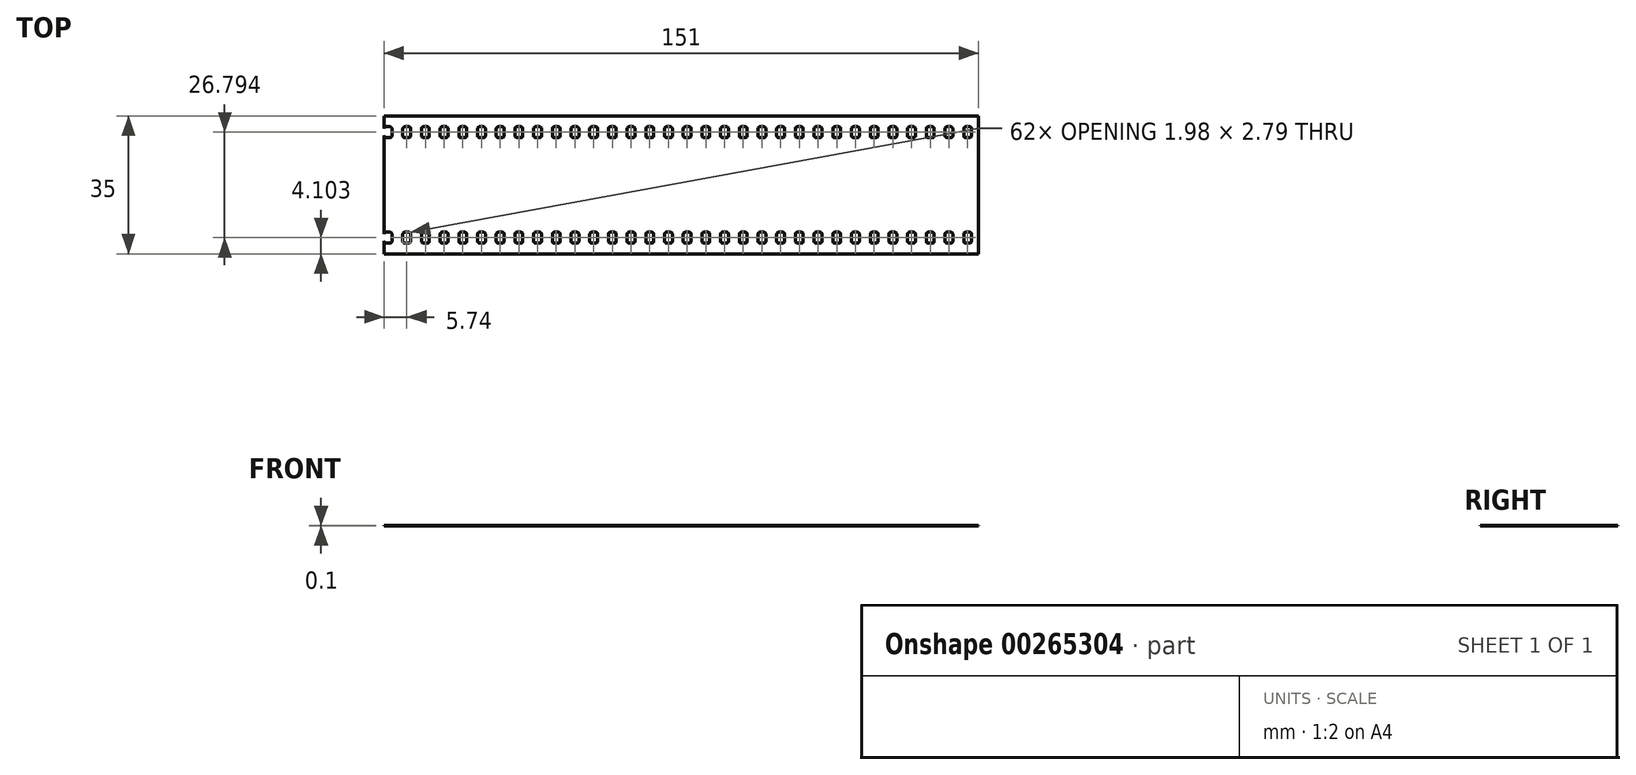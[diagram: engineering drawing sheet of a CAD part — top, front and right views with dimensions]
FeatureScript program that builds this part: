
annotation { "Feature Type Name" : "Feature", "Feature Type Description" : "" }
export const myFeature = defineFeature(function(context is Context, id is Id, definition is map)
    precondition{}
    {
        {
            var Q0;
            Q0=qCreatedBy(makeId("Top.planeOp"),FACE);
            var sketch = newSketch(context, id + "F0", { "sketchPlane" : qUnion([Q0])});
            skLineSegment(sketch, "E0.bottom", {"start": v(0, 0) * mm, "end": v(151, 0) * mm});
            skLineSegment(sketch, "E0.top", {"start": v(0, -35) * mm, "end": v(151, -35) * mm});
            skLineSegment(sketch, "E0.left", {"start": v(0, 0) * mm, "end": v(0, -35) * mm});
            skLineSegment(sketch, "E0.right", {"start": v(151, 0) * mm, "end": v(151, -35) * mm});
            skLineSegment(sketch, "E1.bottom", {"start": v(0.5, -2.7) * mm, "end": v(1.47, -2.7) * mm});
            skLineSegment(sketch, "E1.top", {"start": v(0.5, -5.5) * mm, "end": v(1.47, -5.5) * mm});
            skLineSegment(sketch, "E1.left", {"start": v(0, -3.22) * mm, "end": v(0, -5) * mm});
            skLineSegment(sketch, "E1.right", {"start": v(1.98, -3.22) * mm, "end": v(1.98, -4.99) * mm});
            skPoint(sketch, "E2.visualSharp", {"position": v(0, -2.7) * mm});
            skArc(sketch, "E2.filletArc", {"start": v(0.5, -2.7) * mm, "mid": v(0.15, -2.86) * mm, "end": v(0, -3.22) * mm});
            skPoint(sketch, "E3.visualSharp", {"position": v(1.98, -2.7) * mm});
            skArc(sketch, "E3.filletArc", {"start": v(1.98, -3.22) * mm, "mid": v(1.83, -2.86) * mm, "end": v(1.47, -2.7) * mm});
            skPoint(sketch, "E4.visualSharp", {"position": v(1.98, -5.5) * mm});
            skArc(sketch, "E4.filletArc", {"start": v(1.47, -5.5) * mm, "mid": v(1.83, -5.35) * mm, "end": v(1.98, -4.99) * mm});
            skPoint(sketch, "E5.visualSharp", {"position": v(0, -5.5) * mm});
            skArc(sketch, "E5.filletArc", {"start": v(0, -5) * mm, "mid": v(0.15, -5.35) * mm, "end": v(0.5, -5.5) * mm});
            skPoint(sketch, "E6.0.1.0", {"position": v(0, -32.3) * mm});
            skPoint(sketch, "E6.0.1.1", {"position": v(1.98, -29.5) * mm});
            skPoint(sketch, "E6.0.1.2", {"position": v(0, -29.5) * mm});
            skPoint(sketch, "E6.0.1.3", {"position": v(1.98, -32.3) * mm});
            skLineSegment(sketch, "E6.0.1.4", {"start": v(0.5, -29.5) * mm, "end": v(1.47, -29.5) * mm});
            skLineSegment(sketch, "E6.0.1.5", {"start": v(0.5, -32.3) * mm, "end": v(1.47, -32.3) * mm});
            skLineSegment(sketch, "E6.0.1.6", {"start": v(0, -30) * mm, "end": v(0, -31.78) * mm});
            skLineSegment(sketch, "E6.0.1.7", {"start": v(1.98, -30.01) * mm, "end": v(1.98, -31.78) * mm});
            skArc(sketch, "E6.0.1.8", {"start": v(0.5, -29.5) * mm, "mid": v(0.15, -29.65) * mm, "end": v(0, -30) * mm});
            skArc(sketch, "E6.0.1.9", {"start": v(1.98, -30.01) * mm, "mid": v(1.83, -29.65) * mm, "end": v(1.47, -29.5) * mm});
            skArc(sketch, "E6.0.1.10", {"start": v(1.47, -32.3) * mm, "mid": v(1.83, -32.14) * mm, "end": v(1.98, -31.78) * mm});
            skArc(sketch, "E6.0.1.11", {"start": v(0, -31.78) * mm, "mid": v(0.15, -32.14) * mm, "end": v(0.5, -32.3) * mm});
            skPoint(sketch, "E6.1.0.0", {"position": v(4.75, -5.5) * mm});
            skPoint(sketch, "E6.1.0.1", {"position": v(6.73, -2.7) * mm});
            skPoint(sketch, "E6.1.0.2", {"position": v(4.75, -2.7) * mm});
            skPoint(sketch, "E6.1.0.3", {"position": v(6.73, -5.5) * mm});
            skLineSegment(sketch, "E6.1.0.4", {"start": v(5.26, -2.7) * mm, "end": v(6.22, -2.7) * mm});
            skLineSegment(sketch, "E6.1.0.5", {"start": v(5.26, -5.5) * mm, "end": v(6.22, -5.5) * mm});
            skLineSegment(sketch, "E6.1.0.6", {"start": v(4.75, -3.22) * mm, "end": v(4.75, -5) * mm});
            skLineSegment(sketch, "E6.1.0.7", {"start": v(6.73, -3.22) * mm, "end": v(6.73, -4.99) * mm});
            skArc(sketch, "E6.1.0.8", {"start": v(5.26, -2.7) * mm, "mid": v(4.9, -2.86) * mm, "end": v(4.75, -3.22) * mm});
            skArc(sketch, "E6.1.0.9", {"start": v(6.73, -3.22) * mm, "mid": v(6.58, -2.86) * mm, "end": v(6.22, -2.7) * mm});
            skArc(sketch, "E6.1.0.10", {"start": v(6.22, -5.5) * mm, "mid": v(6.58, -5.35) * mm, "end": v(6.73, -4.99) * mm});
            skArc(sketch, "E6.1.0.11", {"start": v(4.75, -5) * mm, "mid": v(4.9, -5.35) * mm, "end": v(5.26, -5.5) * mm});
            skPoint(sketch, "E6.1.1.0", {"position": v(4.75, -32.3) * mm});
            skPoint(sketch, "E6.1.1.1", {"position": v(6.73, -29.5) * mm});
            skPoint(sketch, "E6.1.1.2", {"position": v(4.75, -29.5) * mm});
            skPoint(sketch, "E6.1.1.3", {"position": v(6.73, -32.3) * mm});
            skLineSegment(sketch, "E6.1.1.4", {"start": v(5.26, -29.5) * mm, "end": v(6.22, -29.5) * mm});
            skLineSegment(sketch, "E6.1.1.5", {"start": v(5.26, -32.3) * mm, "end": v(6.22, -32.3) * mm});
            skLineSegment(sketch, "E6.1.1.6", {"start": v(4.75, -30) * mm, "end": v(4.75, -31.78) * mm});
            skLineSegment(sketch, "E6.1.1.7", {"start": v(6.73, -30.01) * mm, "end": v(6.73, -31.78) * mm});
            skArc(sketch, "E6.1.1.8", {"start": v(5.26, -29.5) * mm, "mid": v(4.9, -29.65) * mm, "end": v(4.75, -30) * mm});
            skArc(sketch, "E6.1.1.9", {"start": v(6.73, -30.01) * mm, "mid": v(6.58, -29.65) * mm, "end": v(6.22, -29.5) * mm});
            skArc(sketch, "E6.1.1.10", {"start": v(6.22, -32.3) * mm, "mid": v(6.58, -32.14) * mm, "end": v(6.73, -31.78) * mm});
            skArc(sketch, "E6.1.1.11", {"start": v(4.75, -31.78) * mm, "mid": v(4.9, -32.14) * mm, "end": v(5.26, -32.3) * mm});
            skPoint(sketch, "E6.2.0.0", {"position": v(9.5, -5.5) * mm});
            skPoint(sketch, "E6.2.0.1", {"position": v(11.48, -2.7) * mm});
            skPoint(sketch, "E6.2.0.2", {"position": v(9.5, -2.7) * mm});
            skPoint(sketch, "E6.2.0.3", {"position": v(11.48, -5.5) * mm});
            skLineSegment(sketch, "E6.2.0.4", {"start": v(10, -2.7) * mm, "end": v(10.97, -2.7) * mm});
            skLineSegment(sketch, "E6.2.0.5", {"start": v(10, -5.5) * mm, "end": v(10.97, -5.5) * mm});
            skLineSegment(sketch, "E6.2.0.6", {"start": v(9.5, -3.22) * mm, "end": v(9.5, -5) * mm});
            skLineSegment(sketch, "E6.2.0.7", {"start": v(11.48, -3.22) * mm, "end": v(11.48, -4.99) * mm});
            skArc(sketch, "E6.2.0.8", {"start": v(10, -2.7) * mm, "mid": v(9.65, -2.86) * mm, "end": v(9.5, -3.22) * mm});
            skArc(sketch, "E6.2.0.9", {"start": v(11.48, -3.22) * mm, "mid": v(11.33, -2.86) * mm, "end": v(10.97, -2.7) * mm});
            skArc(sketch, "E6.2.0.10", {"start": v(10.97, -5.5) * mm, "mid": v(11.33, -5.35) * mm, "end": v(11.48, -4.99) * mm});
            skArc(sketch, "E6.2.0.11", {"start": v(9.5, -5) * mm, "mid": v(9.65, -5.35) * mm, "end": v(10, -5.5) * mm});
            skPoint(sketch, "E6.2.1.0", {"position": v(9.5, -32.3) * mm});
            skPoint(sketch, "E6.2.1.1", {"position": v(11.48, -29.5) * mm});
            skPoint(sketch, "E6.2.1.2", {"position": v(9.5, -29.5) * mm});
            skPoint(sketch, "E6.2.1.3", {"position": v(11.48, -32.3) * mm});
            skLineSegment(sketch, "E6.2.1.4", {"start": v(10, -29.5) * mm, "end": v(10.97, -29.5) * mm});
            skLineSegment(sketch, "E6.2.1.5", {"start": v(10, -32.3) * mm, "end": v(10.97, -32.3) * mm});
            skLineSegment(sketch, "E6.2.1.6", {"start": v(9.5, -30) * mm, "end": v(9.5, -31.78) * mm});
            skLineSegment(sketch, "E6.2.1.7", {"start": v(11.48, -30.01) * mm, "end": v(11.48, -31.78) * mm});
            skArc(sketch, "E6.2.1.8", {"start": v(10, -29.5) * mm, "mid": v(9.65, -29.65) * mm, "end": v(9.5, -30) * mm});
            skArc(sketch, "E6.2.1.9", {"start": v(11.48, -30.01) * mm, "mid": v(11.33, -29.65) * mm, "end": v(10.97, -29.5) * mm});
            skArc(sketch, "E6.2.1.10", {"start": v(10.97, -32.3) * mm, "mid": v(11.33, -32.14) * mm, "end": v(11.48, -31.78) * mm});
            skArc(sketch, "E6.2.1.11", {"start": v(9.5, -31.78) * mm, "mid": v(9.65, -32.14) * mm, "end": v(10, -32.3) * mm});
            skPoint(sketch, "E6.3.0.0", {"position": v(14.25, -5.5) * mm});
            skPoint(sketch, "E6.3.0.1", {"position": v(16.23, -2.7) * mm});
            skPoint(sketch, "E6.3.0.2", {"position": v(14.25, -2.7) * mm});
            skPoint(sketch, "E6.3.0.3", {"position": v(16.23, -5.5) * mm});
            skLineSegment(sketch, "E6.3.0.4", {"start": v(14.76, -2.7) * mm, "end": v(15.72, -2.7) * mm});
            skLineSegment(sketch, "E6.3.0.5", {"start": v(14.76, -5.5) * mm, "end": v(15.72, -5.5) * mm});
            skLineSegment(sketch, "E6.3.0.6", {"start": v(14.25, -3.22) * mm, "end": v(14.25, -5) * mm});
            skLineSegment(sketch, "E6.3.0.7", {"start": v(16.23, -3.22) * mm, "end": v(16.23, -4.99) * mm});
            skArc(sketch, "E6.3.0.8", {"start": v(14.76, -2.7) * mm, "mid": v(14.4, -2.86) * mm, "end": v(14.25, -3.22) * mm});
            skArc(sketch, "E6.3.0.9", {"start": v(16.23, -3.22) * mm, "mid": v(16.08, -2.86) * mm, "end": v(15.72, -2.7) * mm});
            skArc(sketch, "E6.3.0.10", {"start": v(15.72, -5.5) * mm, "mid": v(16.08, -5.35) * mm, "end": v(16.23, -4.99) * mm});
            skArc(sketch, "E6.3.0.11", {"start": v(14.25, -5) * mm, "mid": v(14.4, -5.35) * mm, "end": v(14.76, -5.5) * mm});
            skPoint(sketch, "E6.3.1.0", {"position": v(14.25, -32.3) * mm});
            skPoint(sketch, "E6.3.1.1", {"position": v(16.23, -29.5) * mm});
            skPoint(sketch, "E6.3.1.2", {"position": v(14.25, -29.5) * mm});
            skPoint(sketch, "E6.3.1.3", {"position": v(16.23, -32.3) * mm});
            skLineSegment(sketch, "E6.3.1.4", {"start": v(14.76, -29.5) * mm, "end": v(15.72, -29.5) * mm});
            skLineSegment(sketch, "E6.3.1.5", {"start": v(14.76, -32.3) * mm, "end": v(15.72, -32.3) * mm});
            skLineSegment(sketch, "E6.3.1.6", {"start": v(14.25, -30) * mm, "end": v(14.25, -31.78) * mm});
            skLineSegment(sketch, "E6.3.1.7", {"start": v(16.23, -30.01) * mm, "end": v(16.23, -31.78) * mm});
            skArc(sketch, "E6.3.1.8", {"start": v(14.76, -29.5) * mm, "mid": v(14.4, -29.65) * mm, "end": v(14.25, -30) * mm});
            skArc(sketch, "E6.3.1.9", {"start": v(16.23, -30.01) * mm, "mid": v(16.08, -29.65) * mm, "end": v(15.72, -29.5) * mm});
            skArc(sketch, "E6.3.1.10", {"start": v(15.72, -32.3) * mm, "mid": v(16.08, -32.14) * mm, "end": v(16.23, -31.78) * mm});
            skArc(sketch, "E6.3.1.11", {"start": v(14.25, -31.78) * mm, "mid": v(14.4, -32.14) * mm, "end": v(14.76, -32.3) * mm});
            skPoint(sketch, "E6.4.0.0", {"position": v(19, -5.5) * mm});
            skPoint(sketch, "E6.4.0.1", {"position": v(20.98, -2.7) * mm});
            skPoint(sketch, "E6.4.0.2", {"position": v(19, -2.7) * mm});
            skPoint(sketch, "E6.4.0.3", {"position": v(20.98, -5.5) * mm});
            skLineSegment(sketch, "E6.4.0.4", {"start": v(19.5, -2.7) * mm, "end": v(20.47, -2.7) * mm});
            skLineSegment(sketch, "E6.4.0.5", {"start": v(19.5, -5.5) * mm, "end": v(20.47, -5.5) * mm});
            skLineSegment(sketch, "E6.4.0.6", {"start": v(19, -3.22) * mm, "end": v(19, -5) * mm});
            skLineSegment(sketch, "E6.4.0.7", {"start": v(20.98, -3.22) * mm, "end": v(20.98, -4.99) * mm});
            skArc(sketch, "E6.4.0.8", {"start": v(19.5, -2.7) * mm, "mid": v(19.15, -2.86) * mm, "end": v(19, -3.22) * mm});
            skArc(sketch, "E6.4.0.9", {"start": v(20.98, -3.22) * mm, "mid": v(20.83, -2.86) * mm, "end": v(20.47, -2.7) * mm});
            skArc(sketch, "E6.4.0.10", {"start": v(20.47, -5.5) * mm, "mid": v(20.83, -5.35) * mm, "end": v(20.98, -4.99) * mm});
            skArc(sketch, "E6.4.0.11", {"start": v(19, -5) * mm, "mid": v(19.15, -5.35) * mm, "end": v(19.5, -5.5) * mm});
            skPoint(sketch, "E6.4.1.0", {"position": v(19, -32.3) * mm});
            skPoint(sketch, "E6.4.1.1", {"position": v(20.98, -29.5) * mm});
            skPoint(sketch, "E6.4.1.2", {"position": v(19, -29.5) * mm});
            skPoint(sketch, "E6.4.1.3", {"position": v(20.98, -32.3) * mm});
            skLineSegment(sketch, "E6.4.1.4", {"start": v(19.5, -29.5) * mm, "end": v(20.47, -29.5) * mm});
            skLineSegment(sketch, "E6.4.1.5", {"start": v(19.5, -32.3) * mm, "end": v(20.47, -32.3) * mm});
            skLineSegment(sketch, "E6.4.1.6", {"start": v(19, -30) * mm, "end": v(19, -31.78) * mm});
            skLineSegment(sketch, "E6.4.1.7", {"start": v(20.98, -30.01) * mm, "end": v(20.98, -31.78) * mm});
            skArc(sketch, "E6.4.1.8", {"start": v(19.5, -29.5) * mm, "mid": v(19.15, -29.65) * mm, "end": v(19, -30) * mm});
            skArc(sketch, "E6.4.1.9", {"start": v(20.98, -30.01) * mm, "mid": v(20.83, -29.65) * mm, "end": v(20.47, -29.5) * mm});
            skArc(sketch, "E6.4.1.10", {"start": v(20.47, -32.3) * mm, "mid": v(20.83, -32.14) * mm, "end": v(20.98, -31.78) * mm});
            skArc(sketch, "E6.4.1.11", {"start": v(19, -31.78) * mm, "mid": v(19.15, -32.14) * mm, "end": v(19.5, -32.3) * mm});
            skPoint(sketch, "E6.5.0.0", {"position": v(23.75, -5.5) * mm});
            skPoint(sketch, "E6.5.0.1", {"position": v(25.73, -2.7) * mm});
            skPoint(sketch, "E6.5.0.2", {"position": v(23.75, -2.7) * mm});
            skPoint(sketch, "E6.5.0.3", {"position": v(25.73, -5.5) * mm});
            skLineSegment(sketch, "E6.5.0.4", {"start": v(24.26, -2.7) * mm, "end": v(25.22, -2.7) * mm});
            skLineSegment(sketch, "E6.5.0.5", {"start": v(24.26, -5.5) * mm, "end": v(25.22, -5.5) * mm});
            skLineSegment(sketch, "E6.5.0.6", {"start": v(23.75, -3.22) * mm, "end": v(23.75, -5) * mm});
            skLineSegment(sketch, "E6.5.0.7", {"start": v(25.73, -3.22) * mm, "end": v(25.73, -4.99) * mm});
            skArc(sketch, "E6.5.0.8", {"start": v(24.26, -2.7) * mm, "mid": v(23.9, -2.86) * mm, "end": v(23.75, -3.22) * mm});
            skArc(sketch, "E6.5.0.9", {"start": v(25.73, -3.22) * mm, "mid": v(25.58, -2.86) * mm, "end": v(25.22, -2.7) * mm});
            skArc(sketch, "E6.5.0.10", {"start": v(25.22, -5.5) * mm, "mid": v(25.58, -5.35) * mm, "end": v(25.73, -4.99) * mm});
            skArc(sketch, "E6.5.0.11", {"start": v(23.75, -5) * mm, "mid": v(23.9, -5.35) * mm, "end": v(24.26, -5.5) * mm});
            skPoint(sketch, "E6.5.1.0", {"position": v(23.75, -32.3) * mm});
            skPoint(sketch, "E6.5.1.1", {"position": v(25.73, -29.5) * mm});
            skPoint(sketch, "E6.5.1.2", {"position": v(23.75, -29.5) * mm});
            skPoint(sketch, "E6.5.1.3", {"position": v(25.73, -32.3) * mm});
            skLineSegment(sketch, "E6.5.1.4", {"start": v(24.26, -29.5) * mm, "end": v(25.22, -29.5) * mm});
            skLineSegment(sketch, "E6.5.1.5", {"start": v(24.26, -32.3) * mm, "end": v(25.22, -32.3) * mm});
            skLineSegment(sketch, "E6.5.1.6", {"start": v(23.75, -30) * mm, "end": v(23.75, -31.78) * mm});
            skLineSegment(sketch, "E6.5.1.7", {"start": v(25.73, -30.01) * mm, "end": v(25.73, -31.78) * mm});
            skArc(sketch, "E6.5.1.8", {"start": v(24.26, -29.5) * mm, "mid": v(23.9, -29.65) * mm, "end": v(23.75, -30) * mm});
            skArc(sketch, "E6.5.1.9", {"start": v(25.73, -30.01) * mm, "mid": v(25.58, -29.65) * mm, "end": v(25.22, -29.5) * mm});
            skArc(sketch, "E6.5.1.10", {"start": v(25.22, -32.3) * mm, "mid": v(25.58, -32.14) * mm, "end": v(25.73, -31.78) * mm});
            skArc(sketch, "E6.5.1.11", {"start": v(23.75, -31.78) * mm, "mid": v(23.9, -32.14) * mm, "end": v(24.26, -32.3) * mm});
            skPoint(sketch, "E6.6.0.0", {"position": v(28.5, -5.5) * mm});
            skPoint(sketch, "E6.6.0.1", {"position": v(30.48, -2.7) * mm});
            skPoint(sketch, "E6.6.0.2", {"position": v(28.5, -2.7) * mm});
            skPoint(sketch, "E6.6.0.3", {"position": v(30.48, -5.5) * mm});
            skLineSegment(sketch, "E6.6.0.4", {"start": v(29, -2.7) * mm, "end": v(29.97, -2.7) * mm});
            skLineSegment(sketch, "E6.6.0.5", {"start": v(29, -5.5) * mm, "end": v(29.97, -5.5) * mm});
            skLineSegment(sketch, "E6.6.0.6", {"start": v(28.5, -3.22) * mm, "end": v(28.5, -5) * mm});
            skLineSegment(sketch, "E6.6.0.7", {"start": v(30.48, -3.22) * mm, "end": v(30.48, -4.99) * mm});
            skArc(sketch, "E6.6.0.8", {"start": v(29, -2.7) * mm, "mid": v(28.65, -2.86) * mm, "end": v(28.5, -3.22) * mm});
            skArc(sketch, "E6.6.0.9", {"start": v(30.48, -3.22) * mm, "mid": v(30.33, -2.86) * mm, "end": v(29.97, -2.7) * mm});
            skArc(sketch, "E6.6.0.10", {"start": v(29.97, -5.5) * mm, "mid": v(30.33, -5.35) * mm, "end": v(30.48, -4.99) * mm});
            skArc(sketch, "E6.6.0.11", {"start": v(28.5, -5) * mm, "mid": v(28.65, -5.35) * mm, "end": v(29, -5.5) * mm});
            skPoint(sketch, "E6.6.1.0", {"position": v(28.5, -32.3) * mm});
            skPoint(sketch, "E6.6.1.1", {"position": v(30.48, -29.5) * mm});
            skPoint(sketch, "E6.6.1.2", {"position": v(28.5, -29.5) * mm});
            skPoint(sketch, "E6.6.1.3", {"position": v(30.48, -32.3) * mm});
            skLineSegment(sketch, "E6.6.1.4", {"start": v(29, -29.5) * mm, "end": v(29.97, -29.5) * mm});
            skLineSegment(sketch, "E6.6.1.5", {"start": v(29, -32.3) * mm, "end": v(29.97, -32.3) * mm});
            skLineSegment(sketch, "E6.6.1.6", {"start": v(28.5, -30) * mm, "end": v(28.5, -31.78) * mm});
            skLineSegment(sketch, "E6.6.1.7", {"start": v(30.48, -30.01) * mm, "end": v(30.48, -31.78) * mm});
            skArc(sketch, "E6.6.1.8", {"start": v(29, -29.5) * mm, "mid": v(28.65, -29.65) * mm, "end": v(28.5, -30) * mm});
            skArc(sketch, "E6.6.1.9", {"start": v(30.48, -30.01) * mm, "mid": v(30.33, -29.65) * mm, "end": v(29.97, -29.5) * mm});
            skArc(sketch, "E6.6.1.10", {"start": v(29.97, -32.3) * mm, "mid": v(30.33, -32.14) * mm, "end": v(30.48, -31.78) * mm});
            skArc(sketch, "E6.6.1.11", {"start": v(28.5, -31.78) * mm, "mid": v(28.65, -32.14) * mm, "end": v(29, -32.3) * mm});
            skPoint(sketch, "E6.7.0.0", {"position": v(33.25, -5.5) * mm});
            skPoint(sketch, "E6.7.0.1", {"position": v(35.23, -2.7) * mm});
            skPoint(sketch, "E6.7.0.2", {"position": v(33.25, -2.7) * mm});
            skPoint(sketch, "E6.7.0.3", {"position": v(35.23, -5.5) * mm});
            skLineSegment(sketch, "E6.7.0.4", {"start": v(33.76, -2.7) * mm, "end": v(34.72, -2.7) * mm});
            skLineSegment(sketch, "E6.7.0.5", {"start": v(33.76, -5.5) * mm, "end": v(34.72, -5.5) * mm});
            skLineSegment(sketch, "E6.7.0.6", {"start": v(33.25, -3.22) * mm, "end": v(33.25, -5) * mm});
            skLineSegment(sketch, "E6.7.0.7", {"start": v(35.23, -3.22) * mm, "end": v(35.23, -4.99) * mm});
            skArc(sketch, "E6.7.0.8", {"start": v(33.76, -2.7) * mm, "mid": v(33.4, -2.86) * mm, "end": v(33.25, -3.22) * mm});
            skArc(sketch, "E6.7.0.9", {"start": v(35.23, -3.22) * mm, "mid": v(35.08, -2.86) * mm, "end": v(34.72, -2.7) * mm});
            skArc(sketch, "E6.7.0.10", {"start": v(34.72, -5.5) * mm, "mid": v(35.08, -5.35) * mm, "end": v(35.23, -4.99) * mm});
            skArc(sketch, "E6.7.0.11", {"start": v(33.25, -5) * mm, "mid": v(33.4, -5.35) * mm, "end": v(33.76, -5.5) * mm});
            skPoint(sketch, "E6.7.1.0", {"position": v(33.25, -32.3) * mm});
            skPoint(sketch, "E6.7.1.1", {"position": v(35.23, -29.5) * mm});
            skPoint(sketch, "E6.7.1.2", {"position": v(33.25, -29.5) * mm});
            skPoint(sketch, "E6.7.1.3", {"position": v(35.23, -32.3) * mm});
            skLineSegment(sketch, "E6.7.1.4", {"start": v(33.76, -29.5) * mm, "end": v(34.72, -29.5) * mm});
            skLineSegment(sketch, "E6.7.1.5", {"start": v(33.76, -32.3) * mm, "end": v(34.72, -32.3) * mm});
            skLineSegment(sketch, "E6.7.1.6", {"start": v(33.25, -30) * mm, "end": v(33.25, -31.78) * mm});
            skLineSegment(sketch, "E6.7.1.7", {"start": v(35.23, -30.01) * mm, "end": v(35.23, -31.78) * mm});
            skArc(sketch, "E6.7.1.8", {"start": v(33.76, -29.5) * mm, "mid": v(33.4, -29.65) * mm, "end": v(33.25, -30) * mm});
            skArc(sketch, "E6.7.1.9", {"start": v(35.23, -30.01) * mm, "mid": v(35.08, -29.65) * mm, "end": v(34.72, -29.5) * mm});
            skArc(sketch, "E6.7.1.10", {"start": v(34.72, -32.3) * mm, "mid": v(35.08, -32.14) * mm, "end": v(35.23, -31.78) * mm});
            skArc(sketch, "E6.7.1.11", {"start": v(33.25, -31.78) * mm, "mid": v(33.4, -32.14) * mm, "end": v(33.76, -32.3) * mm});
            skPoint(sketch, "E6.8.0.0", {"position": v(38, -5.5) * mm});
            skPoint(sketch, "E6.8.0.1", {"position": v(39.98, -2.7) * mm});
            skPoint(sketch, "E6.8.0.2", {"position": v(38, -2.7) * mm});
            skPoint(sketch, "E6.8.0.3", {"position": v(39.98, -5.5) * mm});
            skLineSegment(sketch, "E6.8.0.4", {"start": v(38.5, -2.7) * mm, "end": v(39.47, -2.7) * mm});
            skLineSegment(sketch, "E6.8.0.5", {"start": v(38.5, -5.5) * mm, "end": v(39.47, -5.5) * mm});
            skLineSegment(sketch, "E6.8.0.6", {"start": v(38, -3.22) * mm, "end": v(38, -5) * mm});
            skLineSegment(sketch, "E6.8.0.7", {"start": v(39.98, -3.22) * mm, "end": v(39.98, -4.99) * mm});
            skArc(sketch, "E6.8.0.8", {"start": v(38.5, -2.7) * mm, "mid": v(38.15, -2.86) * mm, "end": v(38, -3.22) * mm});
            skArc(sketch, "E6.8.0.9", {"start": v(39.98, -3.22) * mm, "mid": v(39.83, -2.86) * mm, "end": v(39.47, -2.7) * mm});
            skArc(sketch, "E6.8.0.10", {"start": v(39.47, -5.5) * mm, "mid": v(39.83, -5.35) * mm, "end": v(39.98, -4.99) * mm});
            skArc(sketch, "E6.8.0.11", {"start": v(38, -5) * mm, "mid": v(38.15, -5.35) * mm, "end": v(38.5, -5.5) * mm});
            skPoint(sketch, "E6.8.1.0", {"position": v(38, -32.3) * mm});
            skPoint(sketch, "E6.8.1.1", {"position": v(39.98, -29.5) * mm});
            skPoint(sketch, "E6.8.1.2", {"position": v(38, -29.5) * mm});
            skPoint(sketch, "E6.8.1.3", {"position": v(39.98, -32.3) * mm});
            skLineSegment(sketch, "E6.8.1.4", {"start": v(38.5, -29.5) * mm, "end": v(39.47, -29.5) * mm});
            skLineSegment(sketch, "E6.8.1.5", {"start": v(38.5, -32.3) * mm, "end": v(39.47, -32.3) * mm});
            skLineSegment(sketch, "E6.8.1.6", {"start": v(38, -30) * mm, "end": v(38, -31.78) * mm});
            skLineSegment(sketch, "E6.8.1.7", {"start": v(39.98, -30.01) * mm, "end": v(39.98, -31.78) * mm});
            skArc(sketch, "E6.8.1.8", {"start": v(38.5, -29.5) * mm, "mid": v(38.15, -29.65) * mm, "end": v(38, -30) * mm});
            skArc(sketch, "E6.8.1.9", {"start": v(39.98, -30.01) * mm, "mid": v(39.83, -29.65) * mm, "end": v(39.47, -29.5) * mm});
            skArc(sketch, "E6.8.1.10", {"start": v(39.47, -32.3) * mm, "mid": v(39.83, -32.14) * mm, "end": v(39.98, -31.78) * mm});
            skArc(sketch, "E6.8.1.11", {"start": v(38, -31.78) * mm, "mid": v(38.15, -32.14) * mm, "end": v(38.5, -32.3) * mm});
            skPoint(sketch, "E6.9.0.0", {"position": v(42.75, -5.5) * mm});
            skPoint(sketch, "E6.9.0.1", {"position": v(44.73, -2.7) * mm});
            skPoint(sketch, "E6.9.0.2", {"position": v(42.75, -2.7) * mm});
            skPoint(sketch, "E6.9.0.3", {"position": v(44.73, -5.5) * mm});
            skLineSegment(sketch, "E6.9.0.4", {"start": v(43.26, -2.7) * mm, "end": v(44.22, -2.7) * mm});
            skLineSegment(sketch, "E6.9.0.5", {"start": v(43.26, -5.5) * mm, "end": v(44.22, -5.5) * mm});
            skLineSegment(sketch, "E6.9.0.6", {"start": v(42.75, -3.22) * mm, "end": v(42.75, -5) * mm});
            skLineSegment(sketch, "E6.9.0.7", {"start": v(44.73, -3.22) * mm, "end": v(44.73, -4.99) * mm});
            skArc(sketch, "E6.9.0.8", {"start": v(43.26, -2.7) * mm, "mid": v(42.9, -2.86) * mm, "end": v(42.75, -3.22) * mm});
            skArc(sketch, "E6.9.0.9", {"start": v(44.73, -3.22) * mm, "mid": v(44.58, -2.86) * mm, "end": v(44.22, -2.7) * mm});
            skArc(sketch, "E6.9.0.10", {"start": v(44.22, -5.5) * mm, "mid": v(44.58, -5.35) * mm, "end": v(44.73, -4.99) * mm});
            skArc(sketch, "E6.9.0.11", {"start": v(42.75, -5) * mm, "mid": v(42.9, -5.35) * mm, "end": v(43.26, -5.5) * mm});
            skPoint(sketch, "E6.9.1.0", {"position": v(42.75, -32.3) * mm});
            skPoint(sketch, "E6.9.1.1", {"position": v(44.73, -29.5) * mm});
            skPoint(sketch, "E6.9.1.2", {"position": v(42.75, -29.5) * mm});
            skPoint(sketch, "E6.9.1.3", {"position": v(44.73, -32.3) * mm});
            skLineSegment(sketch, "E6.9.1.4", {"start": v(43.26, -29.5) * mm, "end": v(44.22, -29.5) * mm});
            skLineSegment(sketch, "E6.9.1.5", {"start": v(43.26, -32.3) * mm, "end": v(44.22, -32.3) * mm});
            skLineSegment(sketch, "E6.9.1.6", {"start": v(42.75, -30) * mm, "end": v(42.75, -31.78) * mm});
            skLineSegment(sketch, "E6.9.1.7", {"start": v(44.73, -30.01) * mm, "end": v(44.73, -31.78) * mm});
            skArc(sketch, "E6.9.1.8", {"start": v(43.26, -29.5) * mm, "mid": v(42.9, -29.65) * mm, "end": v(42.75, -30) * mm});
            skArc(sketch, "E6.9.1.9", {"start": v(44.73, -30.01) * mm, "mid": v(44.58, -29.65) * mm, "end": v(44.22, -29.5) * mm});
            skArc(sketch, "E6.9.1.10", {"start": v(44.22, -32.3) * mm, "mid": v(44.58, -32.14) * mm, "end": v(44.73, -31.78) * mm});
            skArc(sketch, "E6.9.1.11", {"start": v(42.75, -31.78) * mm, "mid": v(42.9, -32.14) * mm, "end": v(43.26, -32.3) * mm});
            skPoint(sketch, "E6.10.0.0", {"position": v(47.5, -5.5) * mm});
            skPoint(sketch, "E6.10.0.1", {"position": v(49.48, -2.7) * mm});
            skPoint(sketch, "E6.10.0.2", {"position": v(47.5, -2.7) * mm});
            skPoint(sketch, "E6.10.0.3", {"position": v(49.48, -5.5) * mm});
            skLineSegment(sketch, "E6.10.0.4", {"start": v(48, -2.7) * mm, "end": v(48.97, -2.7) * mm});
            skLineSegment(sketch, "E6.10.0.5", {"start": v(48, -5.5) * mm, "end": v(48.97, -5.5) * mm});
            skLineSegment(sketch, "E6.10.0.6", {"start": v(47.5, -3.22) * mm, "end": v(47.5, -5) * mm});
            skLineSegment(sketch, "E6.10.0.7", {"start": v(49.48, -3.22) * mm, "end": v(49.48, -4.99) * mm});
            skArc(sketch, "E6.10.0.8", {"start": v(48, -2.7) * mm, "mid": v(47.65, -2.86) * mm, "end": v(47.5, -3.22) * mm});
            skArc(sketch, "E6.10.0.9", {"start": v(49.48, -3.22) * mm, "mid": v(49.33, -2.86) * mm, "end": v(48.97, -2.7) * mm});
            skArc(sketch, "E6.10.0.10", {"start": v(48.97, -5.5) * mm, "mid": v(49.33, -5.35) * mm, "end": v(49.48, -4.99) * mm});
            skArc(sketch, "E6.10.0.11", {"start": v(47.5, -5) * mm, "mid": v(47.65, -5.35) * mm, "end": v(48, -5.5) * mm});
            skPoint(sketch, "E6.10.1.0", {"position": v(47.5, -32.3) * mm});
            skPoint(sketch, "E6.10.1.1", {"position": v(49.48, -29.5) * mm});
            skPoint(sketch, "E6.10.1.2", {"position": v(47.5, -29.5) * mm});
            skPoint(sketch, "E6.10.1.3", {"position": v(49.48, -32.3) * mm});
            skLineSegment(sketch, "E6.10.1.4", {"start": v(48, -29.5) * mm, "end": v(48.97, -29.5) * mm});
            skLineSegment(sketch, "E6.10.1.5", {"start": v(48, -32.3) * mm, "end": v(48.97, -32.3) * mm});
            skLineSegment(sketch, "E6.10.1.6", {"start": v(47.5, -30) * mm, "end": v(47.5, -31.78) * mm});
            skLineSegment(sketch, "E6.10.1.7", {"start": v(49.48, -30.01) * mm, "end": v(49.48, -31.78) * mm});
            skArc(sketch, "E6.10.1.8", {"start": v(48, -29.5) * mm, "mid": v(47.65, -29.65) * mm, "end": v(47.5, -30) * mm});
            skArc(sketch, "E6.10.1.9", {"start": v(49.48, -30.01) * mm, "mid": v(49.33, -29.65) * mm, "end": v(48.97, -29.5) * mm});
            skArc(sketch, "E6.10.1.10", {"start": v(48.97, -32.3) * mm, "mid": v(49.33, -32.14) * mm, "end": v(49.48, -31.78) * mm});
            skArc(sketch, "E6.10.1.11", {"start": v(47.5, -31.78) * mm, "mid": v(47.65, -32.14) * mm, "end": v(48, -32.3) * mm});
            skPoint(sketch, "E6.11.0.0", {"position": v(52.25, -5.5) * mm});
            skPoint(sketch, "E6.11.0.1", {"position": v(54.23, -2.7) * mm});
            skPoint(sketch, "E6.11.0.2", {"position": v(52.25, -2.7) * mm});
            skPoint(sketch, "E6.11.0.3", {"position": v(54.23, -5.5) * mm});
            skLineSegment(sketch, "E6.11.0.4", {"start": v(52.76, -2.7) * mm, "end": v(53.72, -2.7) * mm});
            skLineSegment(sketch, "E6.11.0.5", {"start": v(52.76, -5.5) * mm, "end": v(53.72, -5.5) * mm});
            skLineSegment(sketch, "E6.11.0.6", {"start": v(52.25, -3.22) * mm, "end": v(52.25, -5) * mm});
            skLineSegment(sketch, "E6.11.0.7", {"start": v(54.23, -3.22) * mm, "end": v(54.23, -4.99) * mm});
            skArc(sketch, "E6.11.0.8", {"start": v(52.76, -2.7) * mm, "mid": v(52.4, -2.86) * mm, "end": v(52.25, -3.22) * mm});
            skArc(sketch, "E6.11.0.9", {"start": v(54.23, -3.22) * mm, "mid": v(54.08, -2.86) * mm, "end": v(53.72, -2.7) * mm});
            skArc(sketch, "E6.11.0.10", {"start": v(53.72, -5.5) * mm, "mid": v(54.08, -5.35) * mm, "end": v(54.23, -4.99) * mm});
            skArc(sketch, "E6.11.0.11", {"start": v(52.25, -5) * mm, "mid": v(52.4, -5.35) * mm, "end": v(52.76, -5.5) * mm});
            skPoint(sketch, "E6.11.1.0", {"position": v(52.25, -32.3) * mm});
            skPoint(sketch, "E6.11.1.1", {"position": v(54.23, -29.5) * mm});
            skPoint(sketch, "E6.11.1.2", {"position": v(52.25, -29.5) * mm});
            skPoint(sketch, "E6.11.1.3", {"position": v(54.23, -32.3) * mm});
            skLineSegment(sketch, "E6.11.1.4", {"start": v(52.76, -29.5) * mm, "end": v(53.72, -29.5) * mm});
            skLineSegment(sketch, "E6.11.1.5", {"start": v(52.76, -32.3) * mm, "end": v(53.72, -32.3) * mm});
            skLineSegment(sketch, "E6.11.1.6", {"start": v(52.25, -30) * mm, "end": v(52.25, -31.78) * mm});
            skLineSegment(sketch, "E6.11.1.7", {"start": v(54.23, -30.01) * mm, "end": v(54.23, -31.78) * mm});
            skArc(sketch, "E6.11.1.8", {"start": v(52.76, -29.5) * mm, "mid": v(52.4, -29.65) * mm, "end": v(52.25, -30) * mm});
            skArc(sketch, "E6.11.1.9", {"start": v(54.23, -30.01) * mm, "mid": v(54.08, -29.65) * mm, "end": v(53.72, -29.5) * mm});
            skArc(sketch, "E6.11.1.10", {"start": v(53.72, -32.3) * mm, "mid": v(54.08, -32.14) * mm, "end": v(54.23, -31.78) * mm});
            skArc(sketch, "E6.11.1.11", {"start": v(52.25, -31.78) * mm, "mid": v(52.4, -32.14) * mm, "end": v(52.76, -32.3) * mm});
            skPoint(sketch, "E6.12.0.0", {"position": v(57, -5.5) * mm});
            skPoint(sketch, "E6.12.0.1", {"position": v(58.98, -2.7) * mm});
            skPoint(sketch, "E6.12.0.2", {"position": v(57, -2.7) * mm});
            skPoint(sketch, "E6.12.0.3", {"position": v(58.98, -5.5) * mm});
            skLineSegment(sketch, "E6.12.0.4", {"start": v(57.5, -2.7) * mm, "end": v(58.47, -2.7) * mm});
            skLineSegment(sketch, "E6.12.0.5", {"start": v(57.5, -5.5) * mm, "end": v(58.47, -5.5) * mm});
            skLineSegment(sketch, "E6.12.0.6", {"start": v(57, -3.22) * mm, "end": v(57, -5) * mm});
            skLineSegment(sketch, "E6.12.0.7", {"start": v(58.98, -3.22) * mm, "end": v(58.98, -4.99) * mm});
            skArc(sketch, "E6.12.0.8", {"start": v(57.5, -2.7) * mm, "mid": v(57.15, -2.86) * mm, "end": v(57, -3.22) * mm});
            skArc(sketch, "E6.12.0.9", {"start": v(58.98, -3.22) * mm, "mid": v(58.83, -2.86) * mm, "end": v(58.47, -2.7) * mm});
            skArc(sketch, "E6.12.0.10", {"start": v(58.47, -5.5) * mm, "mid": v(58.83, -5.35) * mm, "end": v(58.98, -4.99) * mm});
            skArc(sketch, "E6.12.0.11", {"start": v(57, -5) * mm, "mid": v(57.15, -5.35) * mm, "end": v(57.5, -5.5) * mm});
            skPoint(sketch, "E6.12.1.0", {"position": v(57, -32.3) * mm});
            skPoint(sketch, "E6.12.1.1", {"position": v(58.98, -29.5) * mm});
            skPoint(sketch, "E6.12.1.2", {"position": v(57, -29.5) * mm});
            skPoint(sketch, "E6.12.1.3", {"position": v(58.98, -32.3) * mm});
            skLineSegment(sketch, "E6.12.1.4", {"start": v(57.5, -29.5) * mm, "end": v(58.47, -29.5) * mm});
            skLineSegment(sketch, "E6.12.1.5", {"start": v(57.5, -32.3) * mm, "end": v(58.47, -32.3) * mm});
            skLineSegment(sketch, "E6.12.1.6", {"start": v(57, -30) * mm, "end": v(57, -31.78) * mm});
            skLineSegment(sketch, "E6.12.1.7", {"start": v(58.98, -30.01) * mm, "end": v(58.98, -31.78) * mm});
            skArc(sketch, "E6.12.1.8", {"start": v(57.5, -29.5) * mm, "mid": v(57.15, -29.65) * mm, "end": v(57, -30) * mm});
            skArc(sketch, "E6.12.1.9", {"start": v(58.98, -30.01) * mm, "mid": v(58.83, -29.65) * mm, "end": v(58.47, -29.5) * mm});
            skArc(sketch, "E6.12.1.10", {"start": v(58.47, -32.3) * mm, "mid": v(58.83, -32.14) * mm, "end": v(58.98, -31.78) * mm});
            skArc(sketch, "E6.12.1.11", {"start": v(57, -31.78) * mm, "mid": v(57.15, -32.14) * mm, "end": v(57.5, -32.3) * mm});
            skPoint(sketch, "E6.13.0.0", {"position": v(61.75, -5.5) * mm});
            skPoint(sketch, "E6.13.0.1", {"position": v(63.73, -2.7) * mm});
            skPoint(sketch, "E6.13.0.2", {"position": v(61.75, -2.7) * mm});
            skPoint(sketch, "E6.13.0.3", {"position": v(63.73, -5.5) * mm});
            skLineSegment(sketch, "E6.13.0.4", {"start": v(62.26, -2.7) * mm, "end": v(63.22, -2.7) * mm});
            skLineSegment(sketch, "E6.13.0.5", {"start": v(62.26, -5.5) * mm, "end": v(63.22, -5.5) * mm});
            skLineSegment(sketch, "E6.13.0.6", {"start": v(61.75, -3.22) * mm, "end": v(61.75, -5) * mm});
            skLineSegment(sketch, "E6.13.0.7", {"start": v(63.73, -3.22) * mm, "end": v(63.73, -4.99) * mm});
            skArc(sketch, "E6.13.0.8", {"start": v(62.26, -2.7) * mm, "mid": v(61.9, -2.86) * mm, "end": v(61.75, -3.22) * mm});
            skArc(sketch, "E6.13.0.9", {"start": v(63.73, -3.22) * mm, "mid": v(63.58, -2.86) * mm, "end": v(63.22, -2.7) * mm});
            skArc(sketch, "E6.13.0.10", {"start": v(63.22, -5.5) * mm, "mid": v(63.58, -5.35) * mm, "end": v(63.73, -4.99) * mm});
            skArc(sketch, "E6.13.0.11", {"start": v(61.75, -5) * mm, "mid": v(61.9, -5.35) * mm, "end": v(62.26, -5.5) * mm});
            skPoint(sketch, "E6.13.1.0", {"position": v(61.75, -32.3) * mm});
            skPoint(sketch, "E6.13.1.1", {"position": v(63.73, -29.5) * mm});
            skPoint(sketch, "E6.13.1.2", {"position": v(61.75, -29.5) * mm});
            skPoint(sketch, "E6.13.1.3", {"position": v(63.73, -32.3) * mm});
            skLineSegment(sketch, "E6.13.1.4", {"start": v(62.26, -29.5) * mm, "end": v(63.22, -29.5) * mm});
            skLineSegment(sketch, "E6.13.1.5", {"start": v(62.26, -32.3) * mm, "end": v(63.22, -32.3) * mm});
            skLineSegment(sketch, "E6.13.1.6", {"start": v(61.75, -30) * mm, "end": v(61.75, -31.78) * mm});
            skLineSegment(sketch, "E6.13.1.7", {"start": v(63.73, -30.01) * mm, "end": v(63.73, -31.78) * mm});
            skArc(sketch, "E6.13.1.8", {"start": v(62.26, -29.5) * mm, "mid": v(61.9, -29.65) * mm, "end": v(61.75, -30) * mm});
            skArc(sketch, "E6.13.1.9", {"start": v(63.73, -30.01) * mm, "mid": v(63.58, -29.65) * mm, "end": v(63.22, -29.5) * mm});
            skArc(sketch, "E6.13.1.10", {"start": v(63.22, -32.3) * mm, "mid": v(63.58, -32.14) * mm, "end": v(63.73, -31.78) * mm});
            skArc(sketch, "E6.13.1.11", {"start": v(61.75, -31.78) * mm, "mid": v(61.9, -32.14) * mm, "end": v(62.26, -32.3) * mm});
            skPoint(sketch, "E6.14.0.0", {"position": v(66.5, -5.5) * mm});
            skPoint(sketch, "E6.14.0.1", {"position": v(68.48, -2.7) * mm});
            skPoint(sketch, "E6.14.0.2", {"position": v(66.5, -2.7) * mm});
            skPoint(sketch, "E6.14.0.3", {"position": v(68.48, -5.5) * mm});
            skLineSegment(sketch, "E6.14.0.4", {"start": v(67, -2.7) * mm, "end": v(67.97, -2.7) * mm});
            skLineSegment(sketch, "E6.14.0.5", {"start": v(67, -5.5) * mm, "end": v(67.97, -5.5) * mm});
            skLineSegment(sketch, "E6.14.0.6", {"start": v(66.5, -3.22) * mm, "end": v(66.5, -5) * mm});
            skLineSegment(sketch, "E6.14.0.7", {"start": v(68.48, -3.22) * mm, "end": v(68.48, -4.99) * mm});
            skArc(sketch, "E6.14.0.8", {"start": v(67, -2.7) * mm, "mid": v(66.65, -2.86) * mm, "end": v(66.5, -3.22) * mm});
            skArc(sketch, "E6.14.0.9", {"start": v(68.48, -3.22) * mm, "mid": v(68.33, -2.86) * mm, "end": v(67.97, -2.7) * mm});
            skArc(sketch, "E6.14.0.10", {"start": v(67.97, -5.5) * mm, "mid": v(68.33, -5.35) * mm, "end": v(68.48, -4.99) * mm});
            skArc(sketch, "E6.14.0.11", {"start": v(66.5, -5) * mm, "mid": v(66.65, -5.35) * mm, "end": v(67, -5.5) * mm});
            skPoint(sketch, "E6.14.1.0", {"position": v(66.5, -32.3) * mm});
            skPoint(sketch, "E6.14.1.1", {"position": v(68.48, -29.5) * mm});
            skPoint(sketch, "E6.14.1.2", {"position": v(66.5, -29.5) * mm});
            skPoint(sketch, "E6.14.1.3", {"position": v(68.48, -32.3) * mm});
            skLineSegment(sketch, "E6.14.1.4", {"start": v(67, -29.5) * mm, "end": v(67.97, -29.5) * mm});
            skLineSegment(sketch, "E6.14.1.5", {"start": v(67, -32.3) * mm, "end": v(67.97, -32.3) * mm});
            skLineSegment(sketch, "E6.14.1.6", {"start": v(66.5, -30) * mm, "end": v(66.5, -31.78) * mm});
            skLineSegment(sketch, "E6.14.1.7", {"start": v(68.48, -30.01) * mm, "end": v(68.48, -31.78) * mm});
            skArc(sketch, "E6.14.1.8", {"start": v(67, -29.5) * mm, "mid": v(66.65, -29.65) * mm, "end": v(66.5, -30) * mm});
            skArc(sketch, "E6.14.1.9", {"start": v(68.48, -30.01) * mm, "mid": v(68.33, -29.65) * mm, "end": v(67.97, -29.5) * mm});
            skArc(sketch, "E6.14.1.10", {"start": v(67.97, -32.3) * mm, "mid": v(68.33, -32.14) * mm, "end": v(68.48, -31.78) * mm});
            skArc(sketch, "E6.14.1.11", {"start": v(66.5, -31.78) * mm, "mid": v(66.65, -32.14) * mm, "end": v(67, -32.3) * mm});
            skLineSegment(sketch, "E6.direction1", {"start": v(0, -5.5) * mm, "end": v(4.75, -5.5) * mm, "construction": true});
            skLineSegment(sketch, "E6.direction2", {"start": v(0, -5.5) * mm, "end": v(0, -32.3) * mm, "construction": true});
            skLineSegment(sketch, "E7", {"start": v(0, -5.5) * mm, "end": v(0, -29.5) * mm, "construction": true});
            skPoint(sketch, "E8", {"position": v(0, -17.5) * mm});
            skLineSegment(sketch, "E9.bottom", {"start": v(0, -5.5) * mm, "end": v(36, -5.5) * mm, "construction": true});
            skLineSegment(sketch, "E9.top", {"start": v(0, -29.5) * mm, "end": v(36, -29.5) * mm, "construction": true});
            skLineSegment(sketch, "E9.right", {"start": v(36, -5.5) * mm, "end": v(36, -29.5) * mm, "construction": true});
            skPoint(sketch, "E10.0.15.0", {"position": v(71.25, -5.5) * mm});
            skPoint(sketch, "E10.1.15.0", {"position": v(73.23, -2.7) * mm});
            skPoint(sketch, "E10.2.15.0", {"position": v(71.25, -2.7) * mm});
            skPoint(sketch, "E10.3.15.0", {"position": v(73.23, -5.5) * mm});
            skLineSegment(sketch, "E10.4.15.0", {"start": v(71.76, -2.7) * mm, "end": v(72.72, -2.7) * mm});
            skLineSegment(sketch, "E10.7.15.0", {"start": v(71.76, -5.5) * mm, "end": v(72.72, -5.5) * mm});
            skLineSegment(sketch, "E10.10.15.0", {"start": v(71.25, -3.22) * mm, "end": v(71.25, -5) * mm});
            skLineSegment(sketch, "E10.13.15.0", {"start": v(73.23, -3.22) * mm, "end": v(73.23, -4.99) * mm});
            skArc(sketch, "E10.16.15.0", {"start": v(71.76, -2.7) * mm, "mid": v(71.4, -2.86) * mm, "end": v(71.25, -3.22) * mm});
            skArc(sketch, "E10.20.15.0", {"start": v(73.23, -3.22) * mm, "mid": v(73.08, -2.86) * mm, "end": v(72.72, -2.7) * mm});
            skArc(sketch, "E10.24.15.0", {"start": v(72.72, -5.5) * mm, "mid": v(73.08, -5.35) * mm, "end": v(73.23, -4.99) * mm});
            skArc(sketch, "E10.28.15.0", {"start": v(71.25, -5) * mm, "mid": v(71.4, -5.35) * mm, "end": v(71.76, -5.5) * mm});
            skPoint(sketch, "E10.0.15.1", {"position": v(71.25, -32.3) * mm});
            skPoint(sketch, "E10.1.15.1", {"position": v(73.23, -29.5) * mm});
            skPoint(sketch, "E10.2.15.1", {"position": v(71.25, -29.5) * mm});
            skPoint(sketch, "E10.3.15.1", {"position": v(73.23, -32.3) * mm});
            skLineSegment(sketch, "E10.4.15.1", {"start": v(71.76, -29.5) * mm, "end": v(72.72, -29.5) * mm});
            skLineSegment(sketch, "E10.7.15.1", {"start": v(71.76, -32.3) * mm, "end": v(72.72, -32.3) * mm});
            skLineSegment(sketch, "E10.10.15.1", {"start": v(71.25, -30) * mm, "end": v(71.25, -31.78) * mm});
            skLineSegment(sketch, "E10.13.15.1", {"start": v(73.23, -30.01) * mm, "end": v(73.23, -31.78) * mm});
            skArc(sketch, "E10.16.15.1", {"start": v(71.76, -29.5) * mm, "mid": v(71.4, -29.65) * mm, "end": v(71.25, -30) * mm});
            skArc(sketch, "E10.20.15.1", {"start": v(73.23, -30.01) * mm, "mid": v(73.08, -29.65) * mm, "end": v(72.72, -29.5) * mm});
            skArc(sketch, "E10.24.15.1", {"start": v(72.72, -32.3) * mm, "mid": v(73.08, -32.14) * mm, "end": v(73.23, -31.78) * mm});
            skArc(sketch, "E10.28.15.1", {"start": v(71.25, -31.78) * mm, "mid": v(71.4, -32.14) * mm, "end": v(71.76, -32.3) * mm});
            skPoint(sketch, "E10.0.16.0", {"position": v(76, -5.5) * mm});
            skPoint(sketch, "E10.1.16.0", {"position": v(77.98, -2.7) * mm});
            skPoint(sketch, "E10.2.16.0", {"position": v(76, -2.7) * mm});
            skPoint(sketch, "E10.3.16.0", {"position": v(77.98, -5.5) * mm});
            skLineSegment(sketch, "E10.4.16.0", {"start": v(76.51, -2.7) * mm, "end": v(77.47, -2.7) * mm});
            skLineSegment(sketch, "E10.7.16.0", {"start": v(76.51, -5.5) * mm, "end": v(77.47, -5.5) * mm});
            skLineSegment(sketch, "E10.10.16.0", {"start": v(76, -3.22) * mm, "end": v(76, -5) * mm});
            skLineSegment(sketch, "E10.13.16.0", {"start": v(77.98, -3.22) * mm, "end": v(77.98, -4.99) * mm});
            skArc(sketch, "E10.16.16.0", {"start": v(76.51, -2.7) * mm, "mid": v(76.15, -2.86) * mm, "end": v(76, -3.22) * mm});
            skArc(sketch, "E10.20.16.0", {"start": v(77.98, -3.22) * mm, "mid": v(77.83, -2.86) * mm, "end": v(77.47, -2.7) * mm});
            skArc(sketch, "E10.24.16.0", {"start": v(77.47, -5.5) * mm, "mid": v(77.83, -5.35) * mm, "end": v(77.98, -4.99) * mm});
            skArc(sketch, "E10.28.16.0", {"start": v(76, -5) * mm, "mid": v(76.15, -5.35) * mm, "end": v(76.51, -5.5) * mm});
            skPoint(sketch, "E10.0.16.1", {"position": v(76, -32.3) * mm});
            skPoint(sketch, "E10.1.16.1", {"position": v(77.98, -29.5) * mm});
            skPoint(sketch, "E10.2.16.1", {"position": v(76, -29.5) * mm});
            skPoint(sketch, "E10.3.16.1", {"position": v(77.98, -32.3) * mm});
            skLineSegment(sketch, "E10.4.16.1", {"start": v(76.51, -29.5) * mm, "end": v(77.47, -29.5) * mm});
            skLineSegment(sketch, "E10.7.16.1", {"start": v(76.51, -32.3) * mm, "end": v(77.47, -32.3) * mm});
            skLineSegment(sketch, "E10.10.16.1", {"start": v(76, -30) * mm, "end": v(76, -31.78) * mm});
            skLineSegment(sketch, "E10.13.16.1", {"start": v(77.98, -30.01) * mm, "end": v(77.98, -31.78) * mm});
            skArc(sketch, "E10.16.16.1", {"start": v(76.51, -29.5) * mm, "mid": v(76.15, -29.65) * mm, "end": v(76, -30) * mm});
            skArc(sketch, "E10.20.16.1", {"start": v(77.98, -30.01) * mm, "mid": v(77.83, -29.65) * mm, "end": v(77.47, -29.5) * mm});
            skArc(sketch, "E10.24.16.1", {"start": v(77.47, -32.3) * mm, "mid": v(77.83, -32.14) * mm, "end": v(77.98, -31.78) * mm});
            skArc(sketch, "E10.28.16.1", {"start": v(76, -31.78) * mm, "mid": v(76.15, -32.14) * mm, "end": v(76.51, -32.3) * mm});
            skPoint(sketch, "E10.0.17.0", {"position": v(80.75, -5.5) * mm});
            skPoint(sketch, "E10.1.17.0", {"position": v(82.73, -2.7) * mm});
            skPoint(sketch, "E10.2.17.0", {"position": v(80.75, -2.7) * mm});
            skPoint(sketch, "E10.3.17.0", {"position": v(82.73, -5.5) * mm});
            skLineSegment(sketch, "E10.4.17.0", {"start": v(81.26, -2.7) * mm, "end": v(82.22, -2.7) * mm});
            skLineSegment(sketch, "E10.7.17.0", {"start": v(81.26, -5.5) * mm, "end": v(82.22, -5.5) * mm});
            skLineSegment(sketch, "E10.10.17.0", {"start": v(80.75, -3.22) * mm, "end": v(80.75, -5) * mm});
            skLineSegment(sketch, "E10.13.17.0", {"start": v(82.73, -3.22) * mm, "end": v(82.73, -4.99) * mm});
            skArc(sketch, "E10.16.17.0", {"start": v(81.26, -2.7) * mm, "mid": v(80.9, -2.86) * mm, "end": v(80.75, -3.22) * mm});
            skArc(sketch, "E10.20.17.0", {"start": v(82.73, -3.22) * mm, "mid": v(82.58, -2.86) * mm, "end": v(82.22, -2.7) * mm});
            skArc(sketch, "E10.24.17.0", {"start": v(82.22, -5.5) * mm, "mid": v(82.58, -5.35) * mm, "end": v(82.73, -4.99) * mm});
            skArc(sketch, "E10.28.17.0", {"start": v(80.75, -5) * mm, "mid": v(80.9, -5.35) * mm, "end": v(81.26, -5.5) * mm});
            skPoint(sketch, "E10.0.17.1", {"position": v(80.75, -32.3) * mm});
            skPoint(sketch, "E10.1.17.1", {"position": v(82.73, -29.5) * mm});
            skPoint(sketch, "E10.2.17.1", {"position": v(80.75, -29.5) * mm});
            skPoint(sketch, "E10.3.17.1", {"position": v(82.73, -32.3) * mm});
            skLineSegment(sketch, "E10.4.17.1", {"start": v(81.26, -29.5) * mm, "end": v(82.22, -29.5) * mm});
            skLineSegment(sketch, "E10.7.17.1", {"start": v(81.26, -32.3) * mm, "end": v(82.22, -32.3) * mm});
            skLineSegment(sketch, "E10.10.17.1", {"start": v(80.75, -30) * mm, "end": v(80.75, -31.78) * mm});
            skLineSegment(sketch, "E10.13.17.1", {"start": v(82.73, -30.01) * mm, "end": v(82.73, -31.78) * mm});
            skArc(sketch, "E10.16.17.1", {"start": v(81.26, -29.5) * mm, "mid": v(80.9, -29.65) * mm, "end": v(80.75, -30) * mm});
            skArc(sketch, "E10.20.17.1", {"start": v(82.73, -30.01) * mm, "mid": v(82.58, -29.65) * mm, "end": v(82.22, -29.5) * mm});
            skArc(sketch, "E10.24.17.1", {"start": v(82.22, -32.3) * mm, "mid": v(82.58, -32.14) * mm, "end": v(82.73, -31.78) * mm});
            skArc(sketch, "E10.28.17.1", {"start": v(80.75, -31.78) * mm, "mid": v(80.9, -32.14) * mm, "end": v(81.26, -32.3) * mm});
            skPoint(sketch, "E10.0.18.0", {"position": v(85.5, -5.5) * mm});
            skPoint(sketch, "E10.1.18.0", {"position": v(87.48, -2.7) * mm});
            skPoint(sketch, "E10.2.18.0", {"position": v(85.5, -2.7) * mm});
            skPoint(sketch, "E10.3.18.0", {"position": v(87.48, -5.5) * mm});
            skLineSegment(sketch, "E10.4.18.0", {"start": v(86.01, -2.7) * mm, "end": v(86.97, -2.7) * mm});
            skLineSegment(sketch, "E10.7.18.0", {"start": v(86.01, -5.5) * mm, "end": v(86.97, -5.5) * mm});
            skLineSegment(sketch, "E10.10.18.0", {"start": v(85.5, -3.22) * mm, "end": v(85.5, -5) * mm});
            skLineSegment(sketch, "E10.13.18.0", {"start": v(87.48, -3.22) * mm, "end": v(87.48, -4.99) * mm});
            skArc(sketch, "E10.16.18.0", {"start": v(86.01, -2.7) * mm, "mid": v(85.65, -2.86) * mm, "end": v(85.5, -3.22) * mm});
            skArc(sketch, "E10.20.18.0", {"start": v(87.48, -3.22) * mm, "mid": v(87.33, -2.86) * mm, "end": v(86.97, -2.7) * mm});
            skArc(sketch, "E10.24.18.0", {"start": v(86.97, -5.5) * mm, "mid": v(87.33, -5.35) * mm, "end": v(87.48, -4.99) * mm});
            skArc(sketch, "E10.28.18.0", {"start": v(85.5, -5) * mm, "mid": v(85.65, -5.35) * mm, "end": v(86.01, -5.5) * mm});
            skPoint(sketch, "E10.0.18.1", {"position": v(85.5, -32.3) * mm});
            skPoint(sketch, "E10.1.18.1", {"position": v(87.48, -29.5) * mm});
            skPoint(sketch, "E10.2.18.1", {"position": v(85.5, -29.5) * mm});
            skPoint(sketch, "E10.3.18.1", {"position": v(87.48, -32.3) * mm});
            skLineSegment(sketch, "E10.4.18.1", {"start": v(86.01, -29.5) * mm, "end": v(86.97, -29.5) * mm});
            skLineSegment(sketch, "E10.7.18.1", {"start": v(86.01, -32.3) * mm, "end": v(86.97, -32.3) * mm});
            skLineSegment(sketch, "E10.10.18.1", {"start": v(85.5, -30) * mm, "end": v(85.5, -31.78) * mm});
            skLineSegment(sketch, "E10.13.18.1", {"start": v(87.48, -30.01) * mm, "end": v(87.48, -31.78) * mm});
            skArc(sketch, "E10.16.18.1", {"start": v(86.01, -29.5) * mm, "mid": v(85.65, -29.65) * mm, "end": v(85.5, -30) * mm});
            skArc(sketch, "E10.20.18.1", {"start": v(87.48, -30.01) * mm, "mid": v(87.33, -29.65) * mm, "end": v(86.97, -29.5) * mm});
            skArc(sketch, "E10.24.18.1", {"start": v(86.97, -32.3) * mm, "mid": v(87.33, -32.14) * mm, "end": v(87.48, -31.78) * mm});
            skArc(sketch, "E10.28.18.1", {"start": v(85.5, -31.78) * mm, "mid": v(85.65, -32.14) * mm, "end": v(86.01, -32.3) * mm});
            skPoint(sketch, "E10.0.19.0", {"position": v(90.25, -5.5) * mm});
            skPoint(sketch, "E10.1.19.0", {"position": v(92.23, -2.7) * mm});
            skPoint(sketch, "E10.2.19.0", {"position": v(90.25, -2.7) * mm});
            skPoint(sketch, "E10.3.19.0", {"position": v(92.23, -5.5) * mm});
            skLineSegment(sketch, "E10.4.19.0", {"start": v(90.76, -2.7) * mm, "end": v(91.72, -2.7) * mm});
            skLineSegment(sketch, "E10.7.19.0", {"start": v(90.76, -5.5) * mm, "end": v(91.72, -5.5) * mm});
            skLineSegment(sketch, "E10.10.19.0", {"start": v(90.25, -3.22) * mm, "end": v(90.25, -5) * mm});
            skLineSegment(sketch, "E10.13.19.0", {"start": v(92.23, -3.22) * mm, "end": v(92.23, -4.99) * mm});
            skArc(sketch, "E10.16.19.0", {"start": v(90.76, -2.7) * mm, "mid": v(90.4, -2.86) * mm, "end": v(90.25, -3.22) * mm});
            skArc(sketch, "E10.20.19.0", {"start": v(92.23, -3.22) * mm, "mid": v(92.08, -2.86) * mm, "end": v(91.72, -2.7) * mm});
            skArc(sketch, "E10.24.19.0", {"start": v(91.72, -5.5) * mm, "mid": v(92.08, -5.35) * mm, "end": v(92.23, -4.99) * mm});
            skArc(sketch, "E10.28.19.0", {"start": v(90.25, -5) * mm, "mid": v(90.4, -5.35) * mm, "end": v(90.76, -5.5) * mm});
            skPoint(sketch, "E10.0.19.1", {"position": v(90.25, -32.3) * mm});
            skPoint(sketch, "E10.1.19.1", {"position": v(92.23, -29.5) * mm});
            skPoint(sketch, "E10.2.19.1", {"position": v(90.25, -29.5) * mm});
            skPoint(sketch, "E10.3.19.1", {"position": v(92.23, -32.3) * mm});
            skLineSegment(sketch, "E10.4.19.1", {"start": v(90.76, -29.5) * mm, "end": v(91.72, -29.5) * mm});
            skLineSegment(sketch, "E10.7.19.1", {"start": v(90.76, -32.3) * mm, "end": v(91.72, -32.3) * mm});
            skLineSegment(sketch, "E10.10.19.1", {"start": v(90.25, -30) * mm, "end": v(90.25, -31.78) * mm});
            skLineSegment(sketch, "E10.13.19.1", {"start": v(92.23, -30.01) * mm, "end": v(92.23, -31.78) * mm});
            skArc(sketch, "E10.16.19.1", {"start": v(90.76, -29.5) * mm, "mid": v(90.4, -29.65) * mm, "end": v(90.25, -30) * mm});
            skArc(sketch, "E10.20.19.1", {"start": v(92.23, -30.01) * mm, "mid": v(92.08, -29.65) * mm, "end": v(91.72, -29.5) * mm});
            skArc(sketch, "E10.24.19.1", {"start": v(91.72, -32.3) * mm, "mid": v(92.08, -32.14) * mm, "end": v(92.23, -31.78) * mm});
            skArc(sketch, "E10.28.19.1", {"start": v(90.25, -31.78) * mm, "mid": v(90.4, -32.14) * mm, "end": v(90.76, -32.3) * mm});
            skPoint(sketch, "E10.0.20.0", {"position": v(95, -5.5) * mm});
            skPoint(sketch, "E10.1.20.0", {"position": v(96.98, -2.7) * mm});
            skPoint(sketch, "E10.2.20.0", {"position": v(95, -2.7) * mm});
            skPoint(sketch, "E10.3.20.0", {"position": v(96.98, -5.5) * mm});
            skLineSegment(sketch, "E10.4.20.0", {"start": v(95.51, -2.7) * mm, "end": v(96.47, -2.7) * mm});
            skLineSegment(sketch, "E10.7.20.0", {"start": v(95.51, -5.5) * mm, "end": v(96.47, -5.5) * mm});
            skLineSegment(sketch, "E10.10.20.0", {"start": v(95, -3.22) * mm, "end": v(95, -5) * mm});
            skLineSegment(sketch, "E10.13.20.0", {"start": v(96.98, -3.22) * mm, "end": v(96.98, -4.99) * mm});
            skArc(sketch, "E10.16.20.0", {"start": v(95.51, -2.7) * mm, "mid": v(95.15, -2.86) * mm, "end": v(95, -3.22) * mm});
            skArc(sketch, "E10.20.20.0", {"start": v(96.98, -3.22) * mm, "mid": v(96.83, -2.86) * mm, "end": v(96.47, -2.7) * mm});
            skArc(sketch, "E10.24.20.0", {"start": v(96.47, -5.5) * mm, "mid": v(96.83, -5.35) * mm, "end": v(96.98, -4.99) * mm});
            skArc(sketch, "E10.28.20.0", {"start": v(95, -5) * mm, "mid": v(95.15, -5.35) * mm, "end": v(95.51, -5.5) * mm});
            skPoint(sketch, "E10.0.20.1", {"position": v(95, -32.3) * mm});
            skPoint(sketch, "E10.1.20.1", {"position": v(96.98, -29.5) * mm});
            skPoint(sketch, "E10.2.20.1", {"position": v(95, -29.5) * mm});
            skPoint(sketch, "E10.3.20.1", {"position": v(96.98, -32.3) * mm});
            skLineSegment(sketch, "E10.4.20.1", {"start": v(95.51, -29.5) * mm, "end": v(96.47, -29.5) * mm});
            skLineSegment(sketch, "E10.7.20.1", {"start": v(95.51, -32.3) * mm, "end": v(96.47, -32.3) * mm});
            skLineSegment(sketch, "E10.10.20.1", {"start": v(95, -30) * mm, "end": v(95, -31.78) * mm});
            skLineSegment(sketch, "E10.13.20.1", {"start": v(96.98, -30.01) * mm, "end": v(96.98, -31.78) * mm});
            skArc(sketch, "E10.16.20.1", {"start": v(95.51, -29.5) * mm, "mid": v(95.15, -29.65) * mm, "end": v(95, -30) * mm});
            skArc(sketch, "E10.20.20.1", {"start": v(96.98, -30.01) * mm, "mid": v(96.83, -29.65) * mm, "end": v(96.47, -29.5) * mm});
            skArc(sketch, "E10.24.20.1", {"start": v(96.47, -32.3) * mm, "mid": v(96.83, -32.14) * mm, "end": v(96.98, -31.78) * mm});
            skArc(sketch, "E10.28.20.1", {"start": v(95, -31.78) * mm, "mid": v(95.15, -32.14) * mm, "end": v(95.51, -32.3) * mm});
            skPoint(sketch, "E10.0.21.0", {"position": v(99.75, -5.5) * mm});
            skPoint(sketch, "E10.1.21.0", {"position": v(101.73, -2.7) * mm});
            skPoint(sketch, "E10.2.21.0", {"position": v(99.75, -2.7) * mm});
            skPoint(sketch, "E10.3.21.0", {"position": v(101.73, -5.5) * mm});
            skLineSegment(sketch, "E10.4.21.0", {"start": v(100.26, -2.7) * mm, "end": v(101.22, -2.7) * mm});
            skLineSegment(sketch, "E10.7.21.0", {"start": v(100.26, -5.5) * mm, "end": v(101.22, -5.5) * mm});
            skLineSegment(sketch, "E10.10.21.0", {"start": v(99.75, -3.22) * mm, "end": v(99.75, -5) * mm});
            skLineSegment(sketch, "E10.13.21.0", {"start": v(101.73, -3.22) * mm, "end": v(101.73, -4.99) * mm});
            skArc(sketch, "E10.16.21.0", {"start": v(100.26, -2.7) * mm, "mid": v(99.9, -2.86) * mm, "end": v(99.75, -3.22) * mm});
            skArc(sketch, "E10.20.21.0", {"start": v(101.73, -3.22) * mm, "mid": v(101.58, -2.86) * mm, "end": v(101.22, -2.7) * mm});
            skArc(sketch, "E10.24.21.0", {"start": v(101.22, -5.5) * mm, "mid": v(101.58, -5.35) * mm, "end": v(101.73, -4.99) * mm});
            skArc(sketch, "E10.28.21.0", {"start": v(99.75, -5) * mm, "mid": v(99.9, -5.35) * mm, "end": v(100.26, -5.5) * mm});
            skPoint(sketch, "E10.0.21.1", {"position": v(99.75, -32.3) * mm});
            skPoint(sketch, "E10.1.21.1", {"position": v(101.73, -29.5) * mm});
            skPoint(sketch, "E10.2.21.1", {"position": v(99.75, -29.5) * mm});
            skPoint(sketch, "E10.3.21.1", {"position": v(101.73, -32.3) * mm});
            skLineSegment(sketch, "E10.4.21.1", {"start": v(100.26, -29.5) * mm, "end": v(101.22, -29.5) * mm});
            skLineSegment(sketch, "E10.7.21.1", {"start": v(100.26, -32.3) * mm, "end": v(101.22, -32.3) * mm});
            skLineSegment(sketch, "E10.10.21.1", {"start": v(99.75, -30) * mm, "end": v(99.75, -31.78) * mm});
            skLineSegment(sketch, "E10.13.21.1", {"start": v(101.73, -30.01) * mm, "end": v(101.73, -31.78) * mm});
            skArc(sketch, "E10.16.21.1", {"start": v(100.26, -29.5) * mm, "mid": v(99.9, -29.65) * mm, "end": v(99.75, -30) * mm});
            skArc(sketch, "E10.20.21.1", {"start": v(101.73, -30.01) * mm, "mid": v(101.58, -29.65) * mm, "end": v(101.22, -29.5) * mm});
            skArc(sketch, "E10.24.21.1", {"start": v(101.22, -32.3) * mm, "mid": v(101.58, -32.14) * mm, "end": v(101.73, -31.78) * mm});
            skArc(sketch, "E10.28.21.1", {"start": v(99.75, -31.78) * mm, "mid": v(99.9, -32.14) * mm, "end": v(100.26, -32.3) * mm});
            skPoint(sketch, "E10.0.22.0", {"position": v(104.5, -5.5) * mm});
            skPoint(sketch, "E10.1.22.0", {"position": v(106.48, -2.7) * mm});
            skPoint(sketch, "E10.2.22.0", {"position": v(104.5, -2.7) * mm});
            skPoint(sketch, "E10.3.22.0", {"position": v(106.48, -5.5) * mm});
            skLineSegment(sketch, "E10.4.22.0", {"start": v(105.01, -2.7) * mm, "end": v(105.97, -2.7) * mm});
            skLineSegment(sketch, "E10.7.22.0", {"start": v(105.01, -5.5) * mm, "end": v(105.97, -5.5) * mm});
            skLineSegment(sketch, "E10.10.22.0", {"start": v(104.5, -3.22) * mm, "end": v(104.5, -5) * mm});
            skLineSegment(sketch, "E10.13.22.0", {"start": v(106.48, -3.22) * mm, "end": v(106.48, -4.99) * mm});
            skArc(sketch, "E10.16.22.0", {"start": v(105.01, -2.7) * mm, "mid": v(104.65, -2.86) * mm, "end": v(104.5, -3.22) * mm});
            skArc(sketch, "E10.20.22.0", {"start": v(106.48, -3.22) * mm, "mid": v(106.33, -2.86) * mm, "end": v(105.97, -2.7) * mm});
            skArc(sketch, "E10.24.22.0", {"start": v(105.97, -5.5) * mm, "mid": v(106.33, -5.35) * mm, "end": v(106.48, -4.99) * mm});
            skArc(sketch, "E10.28.22.0", {"start": v(104.5, -5) * mm, "mid": v(104.65, -5.35) * mm, "end": v(105.01, -5.5) * mm});
            skPoint(sketch, "E10.0.22.1", {"position": v(104.5, -32.3) * mm});
            skPoint(sketch, "E10.1.22.1", {"position": v(106.48, -29.5) * mm});
            skPoint(sketch, "E10.2.22.1", {"position": v(104.5, -29.5) * mm});
            skPoint(sketch, "E10.3.22.1", {"position": v(106.48, -32.3) * mm});
            skLineSegment(sketch, "E10.4.22.1", {"start": v(105.01, -29.5) * mm, "end": v(105.97, -29.5) * mm});
            skLineSegment(sketch, "E10.7.22.1", {"start": v(105.01, -32.3) * mm, "end": v(105.97, -32.3) * mm});
            skLineSegment(sketch, "E10.10.22.1", {"start": v(104.5, -30) * mm, "end": v(104.5, -31.78) * mm});
            skLineSegment(sketch, "E10.13.22.1", {"start": v(106.48, -30.01) * mm, "end": v(106.48, -31.78) * mm});
            skArc(sketch, "E10.16.22.1", {"start": v(105.01, -29.5) * mm, "mid": v(104.65, -29.65) * mm, "end": v(104.5, -30) * mm});
            skArc(sketch, "E10.20.22.1", {"start": v(106.48, -30.01) * mm, "mid": v(106.33, -29.65) * mm, "end": v(105.97, -29.5) * mm});
            skArc(sketch, "E10.24.22.1", {"start": v(105.97, -32.3) * mm, "mid": v(106.33, -32.14) * mm, "end": v(106.48, -31.78) * mm});
            skArc(sketch, "E10.28.22.1", {"start": v(104.5, -31.78) * mm, "mid": v(104.65, -32.14) * mm, "end": v(105.01, -32.3) * mm});
            skPoint(sketch, "E10.0.23.0", {"position": v(109.25, -5.5) * mm});
            skPoint(sketch, "E10.1.23.0", {"position": v(111.23, -2.7) * mm});
            skPoint(sketch, "E10.2.23.0", {"position": v(109.25, -2.7) * mm});
            skPoint(sketch, "E10.3.23.0", {"position": v(111.23, -5.5) * mm});
            skLineSegment(sketch, "E10.4.23.0", {"start": v(109.76, -2.7) * mm, "end": v(110.72, -2.7) * mm});
            skLineSegment(sketch, "E10.7.23.0", {"start": v(109.76, -5.5) * mm, "end": v(110.72, -5.5) * mm});
            skLineSegment(sketch, "E10.10.23.0", {"start": v(109.25, -3.22) * mm, "end": v(109.25, -5) * mm});
            skLineSegment(sketch, "E10.13.23.0", {"start": v(111.23, -3.22) * mm, "end": v(111.23, -4.99) * mm});
            skArc(sketch, "E10.16.23.0", {"start": v(109.76, -2.7) * mm, "mid": v(109.4, -2.86) * mm, "end": v(109.25, -3.22) * mm});
            skArc(sketch, "E10.20.23.0", {"start": v(111.23, -3.22) * mm, "mid": v(111.08, -2.86) * mm, "end": v(110.72, -2.7) * mm});
            skArc(sketch, "E10.24.23.0", {"start": v(110.72, -5.5) * mm, "mid": v(111.08, -5.35) * mm, "end": v(111.23, -4.99) * mm});
            skArc(sketch, "E10.28.23.0", {"start": v(109.25, -5) * mm, "mid": v(109.4, -5.35) * mm, "end": v(109.76, -5.5) * mm});
            skPoint(sketch, "E10.0.23.1", {"position": v(109.25, -32.3) * mm});
            skPoint(sketch, "E10.1.23.1", {"position": v(111.23, -29.5) * mm});
            skPoint(sketch, "E10.2.23.1", {"position": v(109.25, -29.5) * mm});
            skPoint(sketch, "E10.3.23.1", {"position": v(111.23, -32.3) * mm});
            skLineSegment(sketch, "E10.4.23.1", {"start": v(109.76, -29.5) * mm, "end": v(110.72, -29.5) * mm});
            skLineSegment(sketch, "E10.7.23.1", {"start": v(109.76, -32.3) * mm, "end": v(110.72, -32.3) * mm});
            skLineSegment(sketch, "E10.10.23.1", {"start": v(109.25, -30) * mm, "end": v(109.25, -31.78) * mm});
            skLineSegment(sketch, "E10.13.23.1", {"start": v(111.23, -30.01) * mm, "end": v(111.23, -31.78) * mm});
            skArc(sketch, "E10.16.23.1", {"start": v(109.76, -29.5) * mm, "mid": v(109.4, -29.65) * mm, "end": v(109.25, -30) * mm});
            skArc(sketch, "E10.20.23.1", {"start": v(111.23, -30.01) * mm, "mid": v(111.08, -29.65) * mm, "end": v(110.72, -29.5) * mm});
            skArc(sketch, "E10.24.23.1", {"start": v(110.72, -32.3) * mm, "mid": v(111.08, -32.14) * mm, "end": v(111.23, -31.78) * mm});
            skArc(sketch, "E10.28.23.1", {"start": v(109.25, -31.78) * mm, "mid": v(109.4, -32.14) * mm, "end": v(109.76, -32.3) * mm});
            skPoint(sketch, "E10.0.24.0", {"position": v(114, -5.5) * mm});
            skPoint(sketch, "E10.1.24.0", {"position": v(115.98, -2.7) * mm});
            skPoint(sketch, "E10.2.24.0", {"position": v(114, -2.7) * mm});
            skPoint(sketch, "E10.3.24.0", {"position": v(115.98, -5.5) * mm});
            skLineSegment(sketch, "E10.4.24.0", {"start": v(114.51, -2.7) * mm, "end": v(115.47, -2.7) * mm});
            skLineSegment(sketch, "E10.7.24.0", {"start": v(114.51, -5.5) * mm, "end": v(115.47, -5.5) * mm});
            skLineSegment(sketch, "E10.10.24.0", {"start": v(114, -3.22) * mm, "end": v(114, -5) * mm});
            skLineSegment(sketch, "E10.13.24.0", {"start": v(115.98, -3.22) * mm, "end": v(115.98, -4.99) * mm});
            skArc(sketch, "E10.16.24.0", {"start": v(114.51, -2.7) * mm, "mid": v(114.15, -2.86) * mm, "end": v(114, -3.22) * mm});
            skArc(sketch, "E10.20.24.0", {"start": v(115.98, -3.22) * mm, "mid": v(115.83, -2.86) * mm, "end": v(115.47, -2.7) * mm});
            skArc(sketch, "E10.24.24.0", {"start": v(115.47, -5.5) * mm, "mid": v(115.83, -5.35) * mm, "end": v(115.98, -4.99) * mm});
            skArc(sketch, "E10.28.24.0", {"start": v(114, -5) * mm, "mid": v(114.15, -5.35) * mm, "end": v(114.51, -5.5) * mm});
            skPoint(sketch, "E10.0.24.1", {"position": v(114, -32.3) * mm});
            skPoint(sketch, "E10.1.24.1", {"position": v(115.98, -29.5) * mm});
            skPoint(sketch, "E10.2.24.1", {"position": v(114, -29.5) * mm});
            skPoint(sketch, "E10.3.24.1", {"position": v(115.98, -32.3) * mm});
            skLineSegment(sketch, "E10.4.24.1", {"start": v(114.51, -29.5) * mm, "end": v(115.47, -29.5) * mm});
            skLineSegment(sketch, "E10.7.24.1", {"start": v(114.51, -32.3) * mm, "end": v(115.47, -32.3) * mm});
            skLineSegment(sketch, "E10.10.24.1", {"start": v(114, -30) * mm, "end": v(114, -31.78) * mm});
            skLineSegment(sketch, "E10.13.24.1", {"start": v(115.98, -30.01) * mm, "end": v(115.98, -31.78) * mm});
            skArc(sketch, "E10.16.24.1", {"start": v(114.51, -29.5) * mm, "mid": v(114.15, -29.65) * mm, "end": v(114, -30) * mm});
            skArc(sketch, "E10.20.24.1", {"start": v(115.98, -30.01) * mm, "mid": v(115.83, -29.65) * mm, "end": v(115.47, -29.5) * mm});
            skArc(sketch, "E10.24.24.1", {"start": v(115.47, -32.3) * mm, "mid": v(115.83, -32.14) * mm, "end": v(115.98, -31.78) * mm});
            skArc(sketch, "E10.28.24.1", {"start": v(114, -31.78) * mm, "mid": v(114.15, -32.14) * mm, "end": v(114.51, -32.3) * mm});
            skPoint(sketch, "E10.0.25.0", {"position": v(118.75, -5.5) * mm});
            skPoint(sketch, "E10.1.25.0", {"position": v(120.73, -2.7) * mm});
            skPoint(sketch, "E10.2.25.0", {"position": v(118.75, -2.7) * mm});
            skPoint(sketch, "E10.3.25.0", {"position": v(120.73, -5.5) * mm});
            skLineSegment(sketch, "E10.4.25.0", {"start": v(119.26, -2.7) * mm, "end": v(120.22, -2.7) * mm});
            skLineSegment(sketch, "E10.7.25.0", {"start": v(119.26, -5.5) * mm, "end": v(120.22, -5.5) * mm});
            skLineSegment(sketch, "E10.10.25.0", {"start": v(118.75, -3.22) * mm, "end": v(118.75, -5) * mm});
            skLineSegment(sketch, "E10.13.25.0", {"start": v(120.73, -3.22) * mm, "end": v(120.73, -4.99) * mm});
            skArc(sketch, "E10.16.25.0", {"start": v(119.26, -2.7) * mm, "mid": v(118.9, -2.86) * mm, "end": v(118.75, -3.22) * mm});
            skArc(sketch, "E10.20.25.0", {"start": v(120.73, -3.22) * mm, "mid": v(120.58, -2.86) * mm, "end": v(120.22, -2.7) * mm});
            skArc(sketch, "E10.24.25.0", {"start": v(120.22, -5.5) * mm, "mid": v(120.58, -5.35) * mm, "end": v(120.73, -4.99) * mm});
            skArc(sketch, "E10.28.25.0", {"start": v(118.75, -5) * mm, "mid": v(118.9, -5.35) * mm, "end": v(119.26, -5.5) * mm});
            skPoint(sketch, "E10.0.25.1", {"position": v(118.75, -32.3) * mm});
            skPoint(sketch, "E10.1.25.1", {"position": v(120.73, -29.5) * mm});
            skPoint(sketch, "E10.2.25.1", {"position": v(118.75, -29.5) * mm});
            skPoint(sketch, "E10.3.25.1", {"position": v(120.73, -32.3) * mm});
            skLineSegment(sketch, "E10.4.25.1", {"start": v(119.26, -29.5) * mm, "end": v(120.22, -29.5) * mm});
            skLineSegment(sketch, "E10.7.25.1", {"start": v(119.26, -32.3) * mm, "end": v(120.22, -32.3) * mm});
            skLineSegment(sketch, "E10.10.25.1", {"start": v(118.75, -30) * mm, "end": v(118.75, -31.78) * mm});
            skLineSegment(sketch, "E10.13.25.1", {"start": v(120.73, -30.01) * mm, "end": v(120.73, -31.78) * mm});
            skArc(sketch, "E10.16.25.1", {"start": v(119.26, -29.5) * mm, "mid": v(118.9, -29.65) * mm, "end": v(118.75, -30) * mm});
            skArc(sketch, "E10.20.25.1", {"start": v(120.73, -30.01) * mm, "mid": v(120.58, -29.65) * mm, "end": v(120.22, -29.5) * mm});
            skArc(sketch, "E10.24.25.1", {"start": v(120.22, -32.3) * mm, "mid": v(120.58, -32.14) * mm, "end": v(120.73, -31.78) * mm});
            skArc(sketch, "E10.28.25.1", {"start": v(118.75, -31.78) * mm, "mid": v(118.9, -32.14) * mm, "end": v(119.26, -32.3) * mm});
            skPoint(sketch, "E10.0.26.0", {"position": v(123.5, -5.5) * mm});
            skPoint(sketch, "E10.1.26.0", {"position": v(125.48, -2.7) * mm});
            skPoint(sketch, "E10.2.26.0", {"position": v(123.5, -2.7) * mm});
            skPoint(sketch, "E10.3.26.0", {"position": v(125.48, -5.5) * mm});
            skLineSegment(sketch, "E10.4.26.0", {"start": v(124.01, -2.7) * mm, "end": v(124.97, -2.7) * mm});
            skLineSegment(sketch, "E10.7.26.0", {"start": v(124.01, -5.5) * mm, "end": v(124.97, -5.5) * mm});
            skLineSegment(sketch, "E10.10.26.0", {"start": v(123.5, -3.22) * mm, "end": v(123.5, -5) * mm});
            skLineSegment(sketch, "E10.13.26.0", {"start": v(125.48, -3.22) * mm, "end": v(125.48, -4.99) * mm});
            skArc(sketch, "E10.16.26.0", {"start": v(124.01, -2.7) * mm, "mid": v(123.65, -2.86) * mm, "end": v(123.5, -3.22) * mm});
            skArc(sketch, "E10.20.26.0", {"start": v(125.48, -3.22) * mm, "mid": v(125.33, -2.86) * mm, "end": v(124.97, -2.7) * mm});
            skArc(sketch, "E10.24.26.0", {"start": v(124.97, -5.5) * mm, "mid": v(125.33, -5.35) * mm, "end": v(125.48, -4.99) * mm});
            skArc(sketch, "E10.28.26.0", {"start": v(123.5, -5) * mm, "mid": v(123.65, -5.35) * mm, "end": v(124.01, -5.5) * mm});
            skPoint(sketch, "E10.0.26.1", {"position": v(123.5, -32.3) * mm});
            skPoint(sketch, "E10.1.26.1", {"position": v(125.48, -29.5) * mm});
            skPoint(sketch, "E10.2.26.1", {"position": v(123.5, -29.5) * mm});
            skPoint(sketch, "E10.3.26.1", {"position": v(125.48, -32.3) * mm});
            skLineSegment(sketch, "E10.4.26.1", {"start": v(124.01, -29.5) * mm, "end": v(124.97, -29.5) * mm});
            skLineSegment(sketch, "E10.7.26.1", {"start": v(124.01, -32.3) * mm, "end": v(124.97, -32.3) * mm});
            skLineSegment(sketch, "E10.10.26.1", {"start": v(123.5, -30) * mm, "end": v(123.5, -31.78) * mm});
            skLineSegment(sketch, "E10.13.26.1", {"start": v(125.48, -30.01) * mm, "end": v(125.48, -31.78) * mm});
            skArc(sketch, "E10.16.26.1", {"start": v(124.01, -29.5) * mm, "mid": v(123.65, -29.65) * mm, "end": v(123.5, -30) * mm});
            skArc(sketch, "E10.20.26.1", {"start": v(125.48, -30.01) * mm, "mid": v(125.33, -29.65) * mm, "end": v(124.97, -29.5) * mm});
            skArc(sketch, "E10.24.26.1", {"start": v(124.97, -32.3) * mm, "mid": v(125.33, -32.14) * mm, "end": v(125.48, -31.78) * mm});
            skArc(sketch, "E10.28.26.1", {"start": v(123.5, -31.78) * mm, "mid": v(123.65, -32.14) * mm, "end": v(124.01, -32.3) * mm});
            skPoint(sketch, "E10.0.27.0", {"position": v(128.25, -5.5) * mm});
            skPoint(sketch, "E10.1.27.0", {"position": v(130.23, -2.7) * mm});
            skPoint(sketch, "E10.2.27.0", {"position": v(128.25, -2.7) * mm});
            skPoint(sketch, "E10.3.27.0", {"position": v(130.23, -5.5) * mm});
            skLineSegment(sketch, "E10.4.27.0", {"start": v(128.76, -2.7) * mm, "end": v(129.72, -2.7) * mm});
            skLineSegment(sketch, "E10.7.27.0", {"start": v(128.76, -5.5) * mm, "end": v(129.72, -5.5) * mm});
            skLineSegment(sketch, "E10.10.27.0", {"start": v(128.25, -3.22) * mm, "end": v(128.25, -5) * mm});
            skLineSegment(sketch, "E10.13.27.0", {"start": v(130.23, -3.22) * mm, "end": v(130.23, -4.99) * mm});
            skArc(sketch, "E10.16.27.0", {"start": v(128.76, -2.7) * mm, "mid": v(128.4, -2.86) * mm, "end": v(128.25, -3.22) * mm});
            skArc(sketch, "E10.20.27.0", {"start": v(130.23, -3.22) * mm, "mid": v(130.08, -2.86) * mm, "end": v(129.72, -2.7) * mm});
            skArc(sketch, "E10.24.27.0", {"start": v(129.72, -5.5) * mm, "mid": v(130.08, -5.35) * mm, "end": v(130.23, -4.99) * mm});
            skArc(sketch, "E10.28.27.0", {"start": v(128.25, -5) * mm, "mid": v(128.4, -5.35) * mm, "end": v(128.76, -5.5) * mm});
            skPoint(sketch, "E10.0.27.1", {"position": v(128.25, -32.3) * mm});
            skPoint(sketch, "E10.1.27.1", {"position": v(130.23, -29.5) * mm});
            skPoint(sketch, "E10.2.27.1", {"position": v(128.25, -29.5) * mm});
            skPoint(sketch, "E10.3.27.1", {"position": v(130.23, -32.3) * mm});
            skLineSegment(sketch, "E10.4.27.1", {"start": v(128.76, -29.5) * mm, "end": v(129.72, -29.5) * mm});
            skLineSegment(sketch, "E10.7.27.1", {"start": v(128.76, -32.3) * mm, "end": v(129.72, -32.3) * mm});
            skLineSegment(sketch, "E10.10.27.1", {"start": v(128.25, -30) * mm, "end": v(128.25, -31.78) * mm});
            skLineSegment(sketch, "E10.13.27.1", {"start": v(130.23, -30.01) * mm, "end": v(130.23, -31.78) * mm});
            skArc(sketch, "E10.16.27.1", {"start": v(128.76, -29.5) * mm, "mid": v(128.4, -29.65) * mm, "end": v(128.25, -30) * mm});
            skArc(sketch, "E10.20.27.1", {"start": v(130.23, -30.01) * mm, "mid": v(130.08, -29.65) * mm, "end": v(129.72, -29.5) * mm});
            skArc(sketch, "E10.24.27.1", {"start": v(129.72, -32.3) * mm, "mid": v(130.08, -32.14) * mm, "end": v(130.23, -31.78) * mm});
            skArc(sketch, "E10.28.27.1", {"start": v(128.25, -31.78) * mm, "mid": v(128.4, -32.14) * mm, "end": v(128.76, -32.3) * mm});
            skPoint(sketch, "E10.0.28.0", {"position": v(133, -5.5) * mm});
            skPoint(sketch, "E10.1.28.0", {"position": v(134.98, -2.7) * mm});
            skPoint(sketch, "E10.2.28.0", {"position": v(133, -2.7) * mm});
            skPoint(sketch, "E10.3.28.0", {"position": v(134.98, -5.5) * mm});
            skLineSegment(sketch, "E10.4.28.0", {"start": v(133.5, -2.7) * mm, "end": v(134.47, -2.7) * mm});
            skLineSegment(sketch, "E10.7.28.0", {"start": v(133.51, -5.5) * mm, "end": v(134.47, -5.5) * mm});
            skLineSegment(sketch, "E10.10.28.0", {"start": v(133, -3.22) * mm, "end": v(133, -5) * mm});
            skLineSegment(sketch, "E10.13.28.0", {"start": v(134.98, -3.22) * mm, "end": v(134.98, -4.99) * mm});
            skArc(sketch, "E10.16.28.0", {"start": v(133.5, -2.7) * mm, "mid": v(133.15, -2.86) * mm, "end": v(133, -3.22) * mm});
            skArc(sketch, "E10.20.28.0", {"start": v(134.98, -3.22) * mm, "mid": v(134.83, -2.86) * mm, "end": v(134.47, -2.7) * mm});
            skArc(sketch, "E10.24.28.0", {"start": v(134.47, -5.5) * mm, "mid": v(134.83, -5.35) * mm, "end": v(134.98, -4.99) * mm});
            skArc(sketch, "E10.28.28.0", {"start": v(133, -5) * mm, "mid": v(133.15, -5.35) * mm, "end": v(133.51, -5.5) * mm});
            skPoint(sketch, "E10.0.28.1", {"position": v(133, -32.3) * mm});
            skPoint(sketch, "E10.1.28.1", {"position": v(134.98, -29.5) * mm});
            skPoint(sketch, "E10.2.28.1", {"position": v(133, -29.5) * mm});
            skPoint(sketch, "E10.3.28.1", {"position": v(134.98, -32.3) * mm});
            skLineSegment(sketch, "E10.4.28.1", {"start": v(133.5, -29.5) * mm, "end": v(134.47, -29.5) * mm});
            skLineSegment(sketch, "E10.7.28.1", {"start": v(133.51, -32.3) * mm, "end": v(134.47, -32.3) * mm});
            skLineSegment(sketch, "E10.10.28.1", {"start": v(133, -30) * mm, "end": v(133, -31.78) * mm});
            skLineSegment(sketch, "E10.13.28.1", {"start": v(134.98, -30.01) * mm, "end": v(134.98, -31.78) * mm});
            skArc(sketch, "E10.16.28.1", {"start": v(133.5, -29.5) * mm, "mid": v(133.15, -29.65) * mm, "end": v(133, -30) * mm});
            skArc(sketch, "E10.20.28.1", {"start": v(134.98, -30.01) * mm, "mid": v(134.83, -29.65) * mm, "end": v(134.47, -29.5) * mm});
            skArc(sketch, "E10.24.28.1", {"start": v(134.47, -32.3) * mm, "mid": v(134.83, -32.14) * mm, "end": v(134.98, -31.78) * mm});
            skArc(sketch, "E10.28.28.1", {"start": v(133, -31.78) * mm, "mid": v(133.15, -32.14) * mm, "end": v(133.51, -32.3) * mm});
            skPoint(sketch, "E10.0.29.0", {"position": v(137.75, -5.5) * mm});
            skPoint(sketch, "E10.1.29.0", {"position": v(139.73, -2.7) * mm});
            skPoint(sketch, "E10.2.29.0", {"position": v(137.75, -2.7) * mm});
            skPoint(sketch, "E10.3.29.0", {"position": v(139.73, -5.5) * mm});
            skLineSegment(sketch, "E10.4.29.0", {"start": v(138.26, -2.7) * mm, "end": v(139.22, -2.7) * mm});
            skLineSegment(sketch, "E10.7.29.0", {"start": v(138.26, -5.5) * mm, "end": v(139.22, -5.5) * mm});
            skLineSegment(sketch, "E10.10.29.0", {"start": v(137.75, -3.22) * mm, "end": v(137.75, -5) * mm});
            skLineSegment(sketch, "E10.13.29.0", {"start": v(139.73, -3.22) * mm, "end": v(139.73, -4.99) * mm});
            skArc(sketch, "E10.16.29.0", {"start": v(138.26, -2.7) * mm, "mid": v(137.9, -2.86) * mm, "end": v(137.75, -3.22) * mm});
            skArc(sketch, "E10.20.29.0", {"start": v(139.73, -3.22) * mm, "mid": v(139.58, -2.86) * mm, "end": v(139.22, -2.7) * mm});
            skArc(sketch, "E10.24.29.0", {"start": v(139.22, -5.5) * mm, "mid": v(139.58, -5.35) * mm, "end": v(139.73, -4.99) * mm});
            skArc(sketch, "E10.28.29.0", {"start": v(137.75, -5) * mm, "mid": v(137.9, -5.35) * mm, "end": v(138.26, -5.5) * mm});
            skPoint(sketch, "E10.0.29.1", {"position": v(137.75, -32.3) * mm});
            skPoint(sketch, "E10.1.29.1", {"position": v(139.73, -29.5) * mm});
            skPoint(sketch, "E10.2.29.1", {"position": v(137.75, -29.5) * mm});
            skPoint(sketch, "E10.3.29.1", {"position": v(139.73, -32.3) * mm});
            skLineSegment(sketch, "E10.4.29.1", {"start": v(138.26, -29.5) * mm, "end": v(139.22, -29.5) * mm});
            skLineSegment(sketch, "E10.7.29.1", {"start": v(138.26, -32.3) * mm, "end": v(139.22, -32.3) * mm});
            skLineSegment(sketch, "E10.10.29.1", {"start": v(137.75, -30) * mm, "end": v(137.75, -31.78) * mm});
            skLineSegment(sketch, "E10.13.29.1", {"start": v(139.73, -30.01) * mm, "end": v(139.73, -31.78) * mm});
            skArc(sketch, "E10.16.29.1", {"start": v(138.26, -29.5) * mm, "mid": v(137.9, -29.65) * mm, "end": v(137.75, -30) * mm});
            skArc(sketch, "E10.20.29.1", {"start": v(139.73, -30.01) * mm, "mid": v(139.58, -29.65) * mm, "end": v(139.22, -29.5) * mm});
            skArc(sketch, "E10.24.29.1", {"start": v(139.22, -32.3) * mm, "mid": v(139.58, -32.14) * mm, "end": v(139.73, -31.78) * mm});
            skArc(sketch, "E10.28.29.1", {"start": v(137.75, -31.78) * mm, "mid": v(137.9, -32.14) * mm, "end": v(138.26, -32.3) * mm});
            skLineSegment(sketch, "E11.1.0.0", {"start": v(74, -5.5) * mm, "end": v(74, -29.5) * mm, "construction": true});
            skLineSegment(sketch, "E11.1.0.1", {"start": v(38, -29.5) * mm, "end": v(74, -29.5) * mm, "construction": true});
            skLineSegment(sketch, "E11.1.0.2", {"start": v(38, -5.5) * mm, "end": v(74, -5.5) * mm, "construction": true});
            skLineSegment(sketch, "E11.1.0.3", {"start": v(38, -5.5) * mm, "end": v(38, -29.5) * mm, "construction": true});
            skLineSegment(sketch, "E11.2.0.0", {"start": v(112, -5.5) * mm, "end": v(112, -29.5) * mm, "construction": true});
            skLineSegment(sketch, "E11.2.0.1", {"start": v(76, -29.5) * mm, "end": v(112, -29.5) * mm, "construction": true});
            skLineSegment(sketch, "E11.2.0.2", {"start": v(76, -5.5) * mm, "end": v(112, -5.5) * mm, "construction": true});
            skLineSegment(sketch, "E11.2.0.3", {"start": v(76, -5.5) * mm, "end": v(76, -29.5) * mm, "construction": true});
            skLineSegment(sketch, "E11.3.0.0", {"start": v(150, -5.5) * mm, "end": v(150, -29.5) * mm, "construction": true});
            skLineSegment(sketch, "E11.3.0.1", {"start": v(114, -29.5) * mm, "end": v(150, -29.5) * mm, "construction": true});
            skLineSegment(sketch, "E11.3.0.2", {"start": v(114, -5.5) * mm, "end": v(150, -5.5) * mm, "construction": true});
            skLineSegment(sketch, "E11.3.0.3", {"start": v(114, -5.5) * mm, "end": v(114, -29.5) * mm, "construction": true});
            skLineSegment(sketch, "E11.direction1", {"start": v(0, -29.5) * mm, "end": v(38, -29.5) * mm, "construction": true});
            skPoint(sketch, "E12.0.30.0", {"position": v(142.5, -5.5) * mm});
            skPoint(sketch, "E12.1.30.0", {"position": v(144.48, -2.7) * mm});
            skPoint(sketch, "E12.2.30.0", {"position": v(142.5, -2.7) * mm});
            skPoint(sketch, "E12.3.30.0", {"position": v(144.48, -5.5) * mm});
            skLineSegment(sketch, "E12.4.30.0", {"start": v(143, -2.7) * mm, "end": v(143.97, -2.7) * mm});
            skLineSegment(sketch, "E12.7.30.0", {"start": v(143.01, -5.5) * mm, "end": v(143.97, -5.5) * mm});
            skLineSegment(sketch, "E12.10.30.0", {"start": v(142.5, -3.22) * mm, "end": v(142.5, -5) * mm});
            skLineSegment(sketch, "E12.13.30.0", {"start": v(144.48, -3.22) * mm, "end": v(144.48, -4.99) * mm});
            skArc(sketch, "E12.16.30.0", {"start": v(143, -2.7) * mm, "mid": v(142.65, -2.86) * mm, "end": v(142.5, -3.22) * mm});
            skArc(sketch, "E12.20.30.0", {"start": v(144.48, -3.22) * mm, "mid": v(144.33, -2.86) * mm, "end": v(143.97, -2.7) * mm});
            skArc(sketch, "E12.24.30.0", {"start": v(143.97, -5.5) * mm, "mid": v(144.33, -5.35) * mm, "end": v(144.48, -4.99) * mm});
            skArc(sketch, "E12.28.30.0", {"start": v(142.5, -5) * mm, "mid": v(142.65, -5.35) * mm, "end": v(143.01, -5.5) * mm});
            skPoint(sketch, "E12.0.30.1", {"position": v(142.5, -32.3) * mm});
            skPoint(sketch, "E12.1.30.1", {"position": v(144.48, -29.5) * mm});
            skPoint(sketch, "E12.2.30.1", {"position": v(142.5, -29.5) * mm});
            skPoint(sketch, "E12.3.30.1", {"position": v(144.48, -32.3) * mm});
            skLineSegment(sketch, "E12.4.30.1", {"start": v(143, -29.5) * mm, "end": v(143.97, -29.5) * mm});
            skLineSegment(sketch, "E12.7.30.1", {"start": v(143.01, -32.3) * mm, "end": v(143.97, -32.3) * mm});
            skLineSegment(sketch, "E12.10.30.1", {"start": v(142.5, -30) * mm, "end": v(142.5, -31.78) * mm});
            skLineSegment(sketch, "E12.13.30.1", {"start": v(144.48, -30.01) * mm, "end": v(144.48, -31.78) * mm});
            skArc(sketch, "E12.16.30.1", {"start": v(143, -29.5) * mm, "mid": v(142.65, -29.65) * mm, "end": v(142.5, -30) * mm});
            skArc(sketch, "E12.20.30.1", {"start": v(144.48, -30.01) * mm, "mid": v(144.33, -29.65) * mm, "end": v(143.97, -29.5) * mm});
            skArc(sketch, "E12.24.30.1", {"start": v(143.97, -32.3) * mm, "mid": v(144.33, -32.14) * mm, "end": v(144.48, -31.78) * mm});
            skArc(sketch, "E12.28.30.1", {"start": v(142.5, -31.78) * mm, "mid": v(142.65, -32.14) * mm, "end": v(143.01, -32.3) * mm});
            skPoint(sketch, "E12.0.31.0", {"position": v(147.25, -5.5) * mm});
            skPoint(sketch, "E12.1.31.0", {"position": v(149.23, -2.7) * mm});
            skPoint(sketch, "E12.2.31.0", {"position": v(147.25, -2.7) * mm});
            skPoint(sketch, "E12.3.31.0", {"position": v(149.23, -5.5) * mm});
            skLineSegment(sketch, "E12.4.31.0", {"start": v(147.76, -2.7) * mm, "end": v(148.72, -2.7) * mm});
            skLineSegment(sketch, "E12.7.31.0", {"start": v(147.76, -5.5) * mm, "end": v(148.72, -5.5) * mm});
            skLineSegment(sketch, "E12.10.31.0", {"start": v(147.25, -3.22) * mm, "end": v(147.25, -5) * mm});
            skLineSegment(sketch, "E12.13.31.0", {"start": v(149.23, -3.22) * mm, "end": v(149.23, -4.99) * mm});
            skArc(sketch, "E12.16.31.0", {"start": v(147.76, -2.7) * mm, "mid": v(147.4, -2.86) * mm, "end": v(147.25, -3.22) * mm});
            skArc(sketch, "E12.20.31.0", {"start": v(149.23, -3.22) * mm, "mid": v(149.08, -2.86) * mm, "end": v(148.72, -2.7) * mm});
            skArc(sketch, "E12.24.31.0", {"start": v(148.72, -5.5) * mm, "mid": v(149.08, -5.35) * mm, "end": v(149.23, -4.99) * mm});
            skArc(sketch, "E12.28.31.0", {"start": v(147.25, -5) * mm, "mid": v(147.4, -5.35) * mm, "end": v(147.76, -5.5) * mm});
            skPoint(sketch, "E12.0.31.1", {"position": v(147.25, -32.3) * mm});
            skPoint(sketch, "E12.1.31.1", {"position": v(149.23, -29.5) * mm});
            skPoint(sketch, "E12.2.31.1", {"position": v(147.25, -29.5) * mm});
            skPoint(sketch, "E12.3.31.1", {"position": v(149.23, -32.3) * mm});
            skLineSegment(sketch, "E12.4.31.1", {"start": v(147.76, -29.5) * mm, "end": v(148.72, -29.5) * mm});
            skLineSegment(sketch, "E12.7.31.1", {"start": v(147.76, -32.3) * mm, "end": v(148.72, -32.3) * mm});
            skLineSegment(sketch, "E12.10.31.1", {"start": v(147.25, -30) * mm, "end": v(147.25, -31.78) * mm});
            skLineSegment(sketch, "E12.13.31.1", {"start": v(149.23, -30.01) * mm, "end": v(149.23, -31.78) * mm});
            skArc(sketch, "E12.16.31.1", {"start": v(147.76, -29.5) * mm, "mid": v(147.4, -29.65) * mm, "end": v(147.25, -30) * mm});
            skArc(sketch, "E12.20.31.1", {"start": v(149.23, -30.01) * mm, "mid": v(149.08, -29.65) * mm, "end": v(148.72, -29.5) * mm});
            skArc(sketch, "E12.24.31.1", {"start": v(148.72, -32.3) * mm, "mid": v(149.08, -32.14) * mm, "end": v(149.23, -31.78) * mm});
            skArc(sketch, "E12.28.31.1", {"start": v(147.25, -31.78) * mm, "mid": v(147.4, -32.14) * mm, "end": v(147.76, -32.3) * mm});
            skSolve(sketch);
        }
        {
            var Q0;
            {var subQ6=sQuery(id+"F0.wireOp",EDGE,"E0.bottom");Q0=makeQuery(id+"F0.imprint","IMPRINT",FACE,{"disambiguationData":[TD([[makeQuery(id+"F0.imprint","IMPRINT",EDGE,{"derivedFrom":subQ6}),-1.0]])]});}
            extrude(context, id + "F1", {"entities" : qUnion([Q0]), "offsetDistance" : 25 * mm, "depth" : 0.1 * mm});
        }
    });
